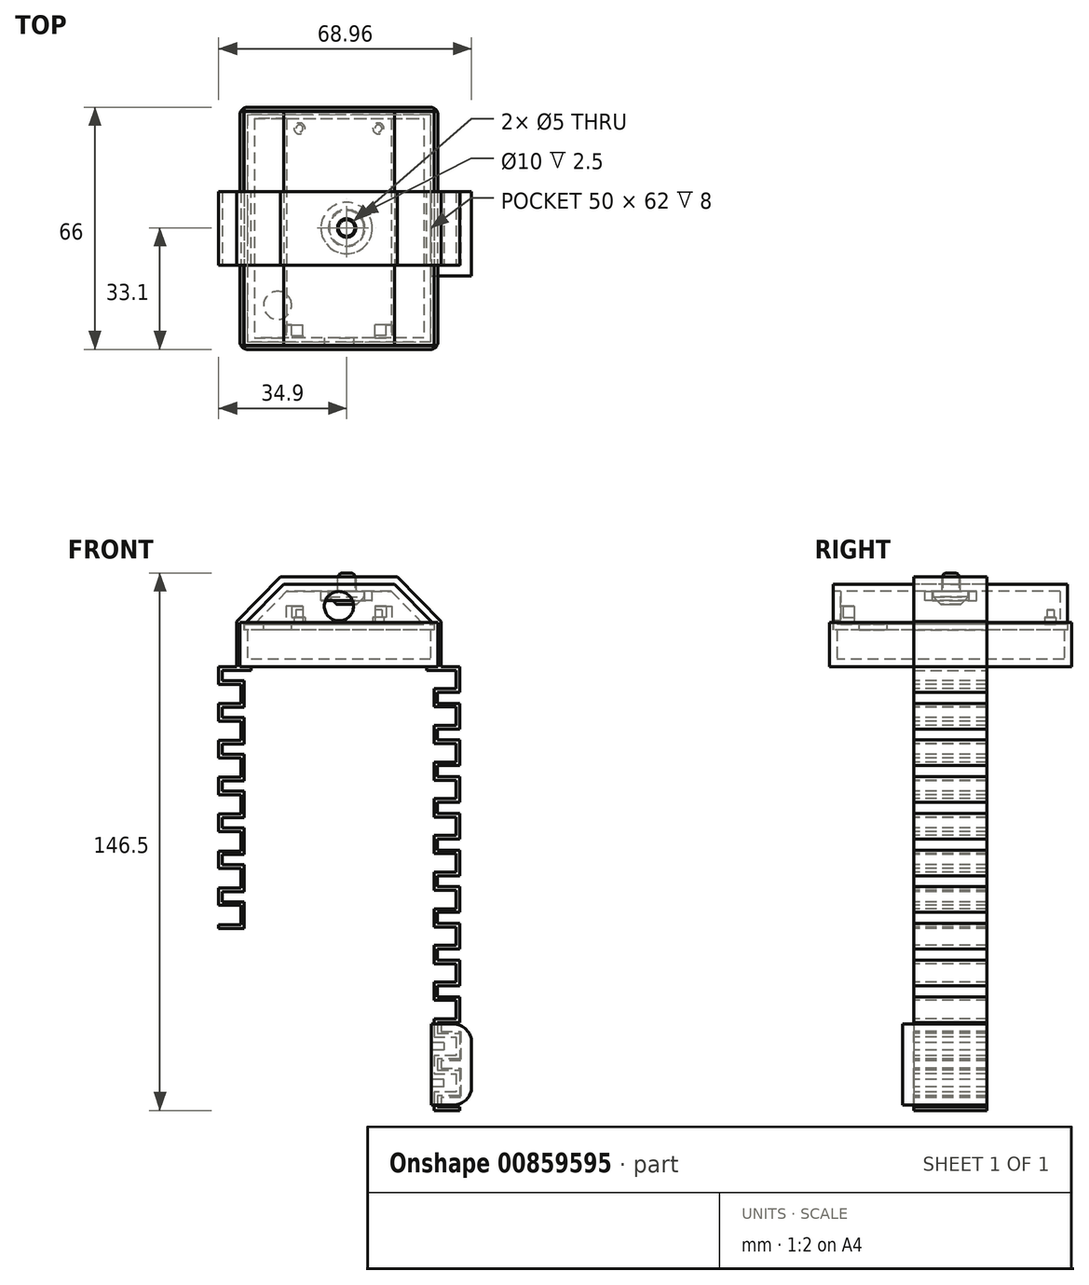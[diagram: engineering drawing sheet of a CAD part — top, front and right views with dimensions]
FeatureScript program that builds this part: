
annotation { "Feature Type Name" : "Feature", "Feature Type Description" : "" }
export const myFeature = defineFeature(function(context is Context, id is Id, definition is map)
    precondition{}
    {
        {
            var Q0;
            Q0=qCreatedBy(makeId("Top.planeOp"),FACE);
            var sketch = newSketch(context, id + "F0", { "sketchPlane" : qUnion([Q0])});
            skLineSegment(sketch, "E0.bottom", {"start": v(27, 33) * mm, "end": v(-27, 33) * mm});
            skLineSegment(sketch, "E0.top", {"start": v(27, -33) * mm, "end": v(-27, -33) * mm});
            skLineSegment(sketch, "E0.left", {"start": v(27, 33) * mm, "end": v(27, -33) * mm});
            skLineSegment(sketch, "E0.right", {"start": v(-27, 33) * mm, "end": v(-27, -33) * mm});
            skPoint(sketch, "E0.middle", {"position": v(0, 0) * mm});
            skSolve(sketch);
        }
        {
            var Q0;
            Q0 = qSketchRegion(id + "F0", true);
            extrude(context, id + "F1", {"entities" : qUnion([Q0]), "depth" : 12 * mm, "offsetDistance" : 25 * mm});
        }
        {
            var Q0;
            Q0=makeQuery(id+"F1.opExtrude","CAP_FACE",FACE,{"disambiguationData":[OSD([sQuery(id+"F0.wireOp",EDGE,"E0.bottom"),sQuery(id+"F0.wireOp",EDGE,"E0.top"),sQuery(id+"F0.wireOp",EDGE,"E0.left"),sQuery(id+"F0.wireOp",EDGE,"E0.right")])],"isStart":false});
            shell(context, id + "F2", {"entities" : qUnion([Q0]), "thickness" : 2 * mm});
        }
        {
            var Q0;
            Q0=makeQuery(id+"F1.opExtrude","CAP_FACE",FACE,{"disambiguationData":[OSD([sQuery(id+"F0.wireOp",EDGE,"E0.bottom"),sQuery(id+"F0.wireOp",EDGE,"E0.top"),sQuery(id+"F0.wireOp",EDGE,"E0.left"),sQuery(id+"F0.wireOp",EDGE,"E0.right")])],"isStart":false});
            var sketch = newSketch(context, id + "F3", { "sketchPlane" : qUnion([Q0])});
            skLineSegment(sketch, "E1.0", {"start": v(25, 31) * mm, "end": v(-25, 31) * mm});
            skLineSegment(sketch, "E2.0", {"start": v(-25, 31) * mm, "end": v(-25, -31) * mm});
            skLineSegment(sketch, "E3.0", {"start": v(25, -31) * mm, "end": v(-25, -31) * mm});
            skLineSegment(sketch, "E4.0", {"start": v(25, 31) * mm, "end": v(25, -31) * mm});
            skLineSegment(sketch, "E5.0", {"start": v(26, 32) * mm, "end": v(-26, 32) * mm});
            skLineSegment(sketch, "E5.1", {"start": v(26, 32) * mm, "end": v(26, -32) * mm});
            skLineSegment(sketch, "E5.2", {"start": v(26, -32) * mm, "end": v(-26, -32) * mm});
            skLineSegment(sketch, "E5.3", {"start": v(-26, 32) * mm, "end": v(-26, -32) * mm});
            skSolve(sketch);
        }
        {
            var Q0;
            Q0 = qSketchRegion(id + "F3", true);
            extrude(context, id + "F4", {"entities" : qUnion([Q0]), "operationType" : NewBodyOperationType.REMOVE, "oppositeDirection" : true, "depth" : 2 * mm, "offsetDistance" : 25 * mm});
        }
        {
            var Q0;
            Q0=makeQuery(id+"F4.boolean.opBoolean","COPY",FACE,{"derivedFrom":makeQuery(id+"F4.opExtrude","CAP_FACE",FACE,{"disambiguationData":[OSD([sQuery(id+"F3.wireOp",EDGE,"E1.0"),sQuery(id+"F3.wireOp",EDGE,"E2.0"),sQuery(id+"F3.wireOp",EDGE,"E3.0"),sQuery(id+"F3.wireOp",EDGE,"E4.0"),sQuery(id+"F3.wireOp",EDGE,"E5.0"),sQuery(id+"F3.wireOp",EDGE,"E5.1"),sQuery(id+"F3.wireOp",EDGE,"E5.2"),sQuery(id+"F3.wireOp",EDGE,"E5.3")])],"isStart":false})});
            var sketch = newSketch(context, id + "F5", { "sketchPlane" : qUnion([Q0])});
            skLineSegment(sketch, "E6.0", {"start": v(25.9, 31.9) * mm, "end": v(-25.9, 31.9) * mm});
            skLineSegment(sketch, "E6.1", {"start": v(25.9, 31.9) * mm, "end": v(25.9, -31.9) * mm});
            skLineSegment(sketch, "E6.2", {"start": v(25.9, -31.9) * mm, "end": v(-25.9, -31.9) * mm});
            skLineSegment(sketch, "E6.3", {"start": v(-25.9, 31.9) * mm, "end": v(-25.9, -31.9) * mm});
            skSolve(sketch);
        }
        {
            var Q0;
            Q0 = qSketchRegion(id + "F5", true);
            extrude(context, id + "F6", {"entities" : qUnion([Q0]), "depth" : 1.5 * mm, "offsetDistance" : 25 * mm});
        }
        {
            var Q0;
            Q0=makeQuery(id+"F6.opExtrude","CAP_FACE",FACE,{"disambiguationData":[OSD([sQuery(id+"F5.wireOp",EDGE,"E6.0"),sQuery(id+"F5.wireOp",EDGE,"E6.1"),sQuery(id+"F5.wireOp",EDGE,"E6.2"),sQuery(id+"F5.wireOp",EDGE,"E6.3")])],"isStart":false});
            var sketch = newSketch(context, id + "F7", { "sketchPlane" : qUnion([Q0])});
            skLineSegment(sketch, "E7.bottom", {"start": v(12.85, 29.25) * mm, "end": v(-12.85, 29.25) * mm, "construction": true});
            skLineSegment(sketch, "E7.top", {"start": v(12.85, -29.25) * mm, "end": v(-12.85, -29.25) * mm, "construction": true});
            skLineSegment(sketch, "E7.left", {"start": v(12.85, 29.25) * mm, "end": v(12.85, -29.25) * mm, "construction": true});
            skLineSegment(sketch, "E7.right", {"start": v(-12.85, 29.25) * mm, "end": v(-12.85, -29.25) * mm, "construction": true});
            skPoint(sketch, "E7.middle", {"position": v(0, 0) * mm});
            skCircle(sketch, "E8", {"center": v(-10.75, 27.25) * mm, "radius": 1.5 * mm});
            skCircle(sketch, "E9.MirrorC", {"center": v(10.75, 27.25) * mm, "radius": 1.5 * mm});
            skLineSegment(sketch, "E10.bottom", {"start": v(-12.85, -29.25) * mm, "end": v(-9.85, -29.25) * mm});
            skLineSegment(sketch, "E10.top", {"start": v(-12.85, -26.25) * mm, "end": v(-9.85, -26.25) * mm});
            skLineSegment(sketch, "E10.left", {"start": v(-12.85, -29.25) * mm, "end": v(-12.85, -26.25) * mm});
            skLineSegment(sketch, "E10.right", {"start": v(-9.85, -29.25) * mm, "end": v(-9.85, -26.25) * mm});
            skLineSegment(sketch, "E11.MirrorCS", {"start": v(12.85, -29.25) * mm, "end": v(9.85, -29.25) * mm});
            skLineSegment(sketch, "E12.MirrorCS", {"start": v(12.85, -29.25) * mm, "end": v(12.85, -26.25) * mm});
            skLineSegment(sketch, "E13.MirrorCS", {"start": v(-12.85, -29.25) * mm, "end": v(12.85, -29.25) * mm, "construction": true});
            skLineSegment(sketch, "E14.MirrorCS", {"start": v(12.85, -26.25) * mm, "end": v(9.85, -26.25) * mm});
            skLineSegment(sketch, "E15.MirrorCS", {"start": v(9.85, -29.25) * mm, "end": v(9.85, -26.25) * mm});
            skSolve(sketch);
        }
        {
            var Q0;
            Q0 = qSketchRegion(id + "F7", true);
            extrude(context, id + "F8", {"entities" : qUnion([Q0]), "operationType" : NewBodyOperationType.ADD, "depth" : 2 * mm, "offsetDistance" : 25 * mm});
        }
        {
            var Q0;
            Q0=makeQuery(id+"F6.opExtrude","CAP_FACE",FACE,{"disambiguationData":[OSD([sQuery(id+"F5.wireOp",EDGE,"E6.0"),sQuery(id+"F5.wireOp",EDGE,"E6.1"),sQuery(id+"F5.wireOp",EDGE,"E6.2"),sQuery(id+"F5.wireOp",EDGE,"E6.3")])],"isStart":false});
            var sketch = newSketch(context, id + "F9", { "sketchPlane" : qUnion([Q0])});
            skLineSegment(sketch, "E16.bottom", {"start": v(-12.85, -26.25) * mm, "end": v(-14.45, -26.25) * mm});
            skLineSegment(sketch, "E16.top", {"start": v(-9.85, -29.9) * mm, "end": v(-14.45, -29.9) * mm});
            skLineSegment(sketch, "E16.left", {"start": v(-9.85, -29.25) * mm, "end": v(-9.85, -29.9) * mm});
            skLineSegment(sketch, "E16.right", {"start": v(-14.45, -26.25) * mm, "end": v(-14.45, -29.9) * mm});
            skLineSegment(sketch, "E17.0", {"start": v(-12.85, -29.25) * mm, "end": v(-12.85, -26.25) * mm});
            skLineSegment(sketch, "E18.0", {"start": v(-12.85, -29.25) * mm, "end": v(-9.85, -29.25) * mm});
            skPoint(sketch, "E19.orphan", {"position": v(-9.85, -26.25) * mm});
            skLineSegment(sketch, "E20.MirrorCS", {"start": v(9.85, -29.25) * mm, "end": v(9.85, -29.9) * mm});
            skLineSegment(sketch, "E21.MirrorCS", {"start": v(14.45, -26.25) * mm, "end": v(14.45, -29.9) * mm});
            skLineSegment(sketch, "E22.MirrorCS", {"start": v(12.85, -29.25) * mm, "end": v(12.85, -26.25) * mm});
            skPoint(sketch, "E23.MirrorP", {"position": v(9.85, -26.25) * mm});
            skLineSegment(sketch, "E24.MirrorCS", {"start": v(9.85, -29.9) * mm, "end": v(14.45, -29.9) * mm});
            skLineSegment(sketch, "E25.MirrorCS", {"start": v(12.85, -26.25) * mm, "end": v(14.45, -26.25) * mm});
            skLineSegment(sketch, "E26.MirrorCS", {"start": v(12.85, -29.25) * mm, "end": v(9.85, -29.25) * mm});
            skSolve(sketch);
        }
        {
            var Q0;
            Q0 = qSketchRegion(id + "F9", true);
            extrude(context, id + "F10", {"entities" : qUnion([Q0]), "operationType" : NewBodyOperationType.ADD, "depth" : 5 * mm, "offsetDistance" : 25 * mm});
        }
        {
            var Q0;
            Q0=makeQuery(id+"F8.opExtrude","CAP_FACE",FACE,{"disambiguationData":[OSD([sQuery(id+"F7.wireOp",EDGE,"E8")])],"isStart":false});
            var sketch = newSketch(context, id + "F11", { "sketchPlane" : qUnion([Q0])});
            skCircle(sketch, "E27", {"center": v(-10.75, 27.25) * mm, "radius": 0.95 * mm});
            skCircle(sketch, "E28.MirrorC", {"center": v(10.75, 27.25) * mm, "radius": 0.95 * mm});
            skSolve(sketch);
        }
        {
            var Q0;
            Q0 = qSketchRegion(id + "F11", true);
            extrude(context, id + "F12", {"entities" : qUnion([Q0]), "operationType" : NewBodyOperationType.ADD, "depth" : 2 * mm, "offsetDistance" : 25 * mm});
        }
        {
            var Q0;
            Q0=makeQuery(id+"F6.opExtrude","SWEPT_FACE",FACE,{"disambiguationData":[OSD([sQuery(id+"F5.wireOp",EDGE,"E6.2")])]});
            var sketch = newSketch(context, id + "F13", { "sketchPlane" : qUnion([Q0])});
            skLineSegment(sketch, "E29.0", {"start": v(25.9, 11.5) * mm, "end": v(-25.9, 11.5) * mm});
            skLineSegment(sketch, "E30", {"start": v(-25.9, 11.5) * mm, "end": v(-15.12, 22.5) * mm});
            skLineSegment(sketch, "E31", {"start": v(-15.12, 22.5) * mm, "end": v(0, 22.5) * mm});
            skLineSegment(sketch, "E32.MirrorCS", {"start": v(15.12, 22.5) * mm, "end": v(0, 22.5) * mm});
            skLineSegment(sketch, "E33.MirrorCS", {"start": v(25.9, 11.5) * mm, "end": v(15.12, 22.5) * mm});
            skSolve(sketch);
        }
        {
            var Q0;
            Q0 = qSketchRegion(id + "F13", true);
            var Q1;
            Q1=makeQuery(id+"F6.opExtrude","SWEPT_FACE",FACE,{"disambiguationData":[OSD([sQuery(id+"F5.wireOp",EDGE,"E6.0")])]});
            extrude(context, id + "F14", {"entities" : qUnion([Q0]), "endBound" : BoundingType.UP_TO_SURFACE, "oppositeDirection" : true, "depth" : 25 * mm, "endBoundEntityFace" : qUnion([Q1]), "offsetDistance" : 25 * mm});
        }
        {
            var Q0;
            Q0=makeQuery(id+"F14.opExtrude","SWEPT_FACE",FACE,{"disambiguationData":[OSD([sQuery(id+"F13.wireOp",EDGE,"E29.0")])]});
            shell(context, id + "F15", {"entities" : qUnion([Q0]), "thickness" : 2 * mm});
        }
        {
            var Q0;
            Q0=makeQuery(id+"F6.opExtrude","CAP_FACE",FACE,{"disambiguationData":[OSD([sQuery(id+"F5.wireOp",EDGE,"E6.0"),sQuery(id+"F5.wireOp",EDGE,"E6.1"),sQuery(id+"F5.wireOp",EDGE,"E6.2"),sQuery(id+"F5.wireOp",EDGE,"E6.3")])],"isStart":false});
            var sketch = newSketch(context, id + "F16", { "sketchPlane" : qUnion([Q0])});
            skCircle(sketch, "E34", {"center": v(-16.73, -20.99) * mm, "radius": 3.81 * mm});
            skSolve(sketch);
        }
        {
            var Q0;
            Q0 = qSketchRegion(id + "F16", true);
            extrude(context, id + "F17", {"entities" : qUnion([Q0]), "operationType" : NewBodyOperationType.REMOVE, "endBound" : BoundingType.UP_TO_NEXT, "oppositeDirection" : true, "depth" : 25 * mm, "offsetDistance" : 25 * mm});
        }
        {
            var Q0;
            Q0=makeQuery(id+"F1.opExtrude","SWEPT_EDGE",EDGE,{"disambiguationData":[OSD([sQuery(id+"F0.wireOp",EDGE,"E0.bottom"),sQuery(id+"F0.wireOp",EDGE,"E0.right")])]});
            var Q1;
            Q1=makeQuery(id+"F1.opExtrude","SWEPT_EDGE",EDGE,{"disambiguationData":[OSD([sQuery(id+"F0.wireOp",EDGE,"E0.bottom"),sQuery(id+"F0.wireOp",EDGE,"E0.left")])]});
            var Q2;
            Q2=makeQuery(id+"F1.opExtrude","SWEPT_EDGE",EDGE,{"disambiguationData":[OSD([sQuery(id+"F0.wireOp",EDGE,"E0.top"),sQuery(id+"F0.wireOp",EDGE,"E0.left")])]});
            var Q3;
            Q3=makeQuery(id+"F1.opExtrude","SWEPT_EDGE",EDGE,{"disambiguationData":[OSD([sQuery(id+"F0.wireOp",EDGE,"E0.top"),sQuery(id+"F0.wireOp",EDGE,"E0.right")])]});
            fillet(context, id + "F18", {"entities" : qUnion([Q0, Q1, Q2, Q3]), "radius" : 2 * mm, "tangentPropagation" : true, "allowEdgeOverflow" : false});
        }
        {
            var Q0;
            Q0=makeQuery(id+"F0.imprint","IMPRINT",FACE,{"disambiguationData":[TD([[makeQuery(id+"F0.imprint","IMPRINT",EDGE,{"derivedFrom":sQuery(id+"F0.wireOp",EDGE,"E0.bottom")}),1.0]])]});
            var sketch = newSketch(context, id + "F19", { "sketchPlane" : qUnion([Q0])});
            skLineSegment(sketch, "E35.0", {"start": v(27, 10) * mm, "end": v(27, -10) * mm});
            skLineSegment(sketch, "E36.0", {"start": v(-27, 10) * mm, "end": v(-27, -10) * mm});
            skLineSegment(sketch, "E37.0", {"start": v(-25.9, 10) * mm, "end": v(-25.9, -10) * mm});
            skLineSegment(sketch, "E38.0", {"start": v(25.9, 10) * mm, "end": v(25.9, -10) * mm});
            skLineSegment(sketch, "E39", {"start": v(-27, -10) * mm, "end": v(-25.9, -10) * mm});
            skLineSegment(sketch, "E40", {"start": v(-27, 10) * mm, "end": v(-25.9, 10) * mm});
            skLineSegment(sketch, "E41.trimOffspring", {"start": v(25.9, -10) * mm, "end": v(27, -10) * mm});
            skLineSegment(sketch, "E42.trimOffspring", {"start": v(25.9, 10) * mm, "end": v(27, 10) * mm});
            skPoint(sketch, "E43.orphan", {"position": v(-25.9, 31.9) * mm});
            skPoint(sketch, "E44.orphan", {"position": v(-27, 33) * mm});
            skPoint(sketch, "E45.orphan", {"position": v(-27, -33) * mm});
            skPoint(sketch, "E46.orphan", {"position": v(-25.9, -31.9) * mm});
            skPoint(sketch, "E47.orphan", {"position": v(27, -33) * mm});
            skPoint(sketch, "E48.orphan", {"position": v(25.9, -31.9) * mm});
            skPoint(sketch, "E49.orphan", {"position": v(27, 33) * mm});
            skPoint(sketch, "E50.orphan", {"position": v(25.9, 31.9) * mm});
            skSolve(sketch);
        }
        {
            var Q0;
            Q0 = qSketchRegion(id + "F19", true);
            extrude(context, id + "F20", {"entities" : qUnion([Q0]), "operationType" : NewBodyOperationType.REMOVE, "endBound" : BoundingType.THROUGH_ALL, "depth" : 25 * mm, "offsetDistance" : 25 * mm});
        }
        {
            var Q0;
            Q0=makeQuery(id+"F20.boolean.opBoolean","COPY",FACE,{"derivedFrom":makeQuery(id+"F20.opExtrude","SWEPT_FACE",FACE,{"disambiguationData":[OSD([sQuery(id+"F19.wireOp",EDGE,"E39")])]})});
            var sketch = newSketch(context, id + "F21", { "sketchPlane" : qUnion([Q0])});
            skLineSegment(sketch, "E51.0", {"start": v(-15.12, 22.5) * mm, "end": v(-25.9, 11.5) * mm});
            skLineSegment(sketch, "E52.0", {"start": v(15.12, 22.5) * mm, "end": v(-15.12, 22.5) * mm});
            skLineSegment(sketch, "E53.0", {"start": v(15.12, 22.5) * mm, "end": v(25.9, 11.5) * mm});
            skLineSegment(sketch, "E54.0", {"start": v(25.9, 10) * mm, "end": v(25.9, 0) * mm});
            skLineSegment(sketch, "E55.0", {"start": v(-25.9, 10) * mm, "end": v(-25.9, 0) * mm});
            skLineSegment(sketch, "E56", {"start": v(-25.9, 11.5) * mm, "end": v(-25.9, 10) * mm});
            skLineSegment(sketch, "E57", {"start": v(25.9, 11.5) * mm, "end": v(25.9, 10) * mm});
            skLineSegment(sketch, "E58", {"start": v(-25.9, 0) * mm, "end": v(-27.9, 0) * mm});
            skLineSegment(sketch, "E59.0", {"start": v(-27.9, 10) * mm, "end": v(-27.9, 0) * mm});
            skLineSegment(sketch, "E59.1", {"start": v(-27.9, 12.32) * mm, "end": v(-27.9, 10) * mm});
            skLineSegment(sketch, "E59.2", {"start": v(-15.96, 24.5) * mm, "end": v(-27.9, 12.32) * mm});
            skLineSegment(sketch, "E59.3", {"start": v(27.9, 10) * mm, "end": v(27.9, 0) * mm});
            skLineSegment(sketch, "E59.4", {"start": v(27.9, 12.32) * mm, "end": v(27.9, 10) * mm});
            skLineSegment(sketch, "E59.5", {"start": v(15.96, 24.5) * mm, "end": v(27.9, 12.32) * mm});
            skLineSegment(sketch, "E59.6", {"start": v(15.96, 24.5) * mm, "end": v(-15.96, 24.5) * mm});
            skLineSegment(sketch, "E60", {"start": v(25.9, 0) * mm, "end": v(27.9, 0) * mm});
            skSolve(sketch);
        }
        {
            var Q0;
            Q0 = qSketchRegion(id + "F21", true);
            var Q1;
            Q1=makeQuery(id+"F20.boolean.opBoolean","COPY",FACE,{"derivedFrom":makeQuery(id+"F20.opExtrude","SWEPT_FACE",FACE,{"disambiguationData":[OSD([sQuery(id+"F19.wireOp",EDGE,"E40")])]})});
            extrude(context, id + "F22", {"entities" : qUnion([Q0]), "endBound" : BoundingType.UP_TO_SURFACE, "depth" : 25 * mm, "endBoundEntityFace" : qUnion([Q1]), "offsetDistance" : 25 * mm});
        }
        {
            var Q0;
            Q0=makeQuery(id+"F14.opExtrude","CAP_FACE",FACE,{"disambiguationData":[OSD([sQuery(id+"F13.wireOp",EDGE,"E29.0"),sQuery(id+"F13.wireOp",EDGE,"E30"),sQuery(id+"F13.wireOp",EDGE,"E31"),sQuery(id+"F13.wireOp",EDGE,"E32.MirrorCS"),sQuery(id+"F13.wireOp",EDGE,"E33.MirrorCS")])],"isStart":true});
            var sketch = newSketch(context, id + "F23", { "sketchPlane" : qUnion([Q0])});
            skCircle(sketch, "E61", {"center": v(0, 16.5) * mm, "radius": 4 * mm});
            skSolve(sketch);
        }
        {
            var Q0;
            Q0 = qSketchRegion(id + "F23", true);
            var Q1;
            {var subQ0=sQuery(id+"F13.wireOp",EDGE,"E33.MirrorCS");var subQ1=sQuery(id+"F13.wireOp",EDGE,"E32.MirrorCS");var subQ2=sQuery(id+"F13.wireOp",EDGE,"E31");var subQ3=sQuery(id+"F13.wireOp",EDGE,"E30");var subQ4=sQuery(id+"F13.wireOp",EDGE,"E29.0");Q1=makeQuery(id+"F15.opShell","OFFSET_FACE",FACE,{"disambiguationData":[OSD([subQ4,subQ3,subQ2,subQ1,subQ0]),TDD([makeQuery(id+"F14.opExtrude","CAP_FACE",FACE,{"disambiguationData":[OSD([subQ4,subQ3,subQ2,subQ1,subQ0])],"isStart":true})])]});}
            extrude(context, id + "F24", {"entities" : qUnion([Q0]), "operationType" : NewBodyOperationType.REMOVE, "endBound" : BoundingType.UP_TO_SURFACE, "oppositeDirection" : true, "depth" : 25 * mm, "endBoundEntityFace" : qUnion([Q1]), "offsetDistance" : 25 * mm});
        }
        {
            var Q0;
            Q0=makeQuery(id+"F15.opShell","OFFSET_FACE",FACE,{"disambiguationData":[OSD([sQuery(id+"F13.wireOp",EDGE,"E31"),sQuery(id+"F13.wireOp",EDGE,"E32.MirrorCS")])]});
            var sketch = newSketch(context, id + "F25", { "sketchPlane" : qUnion([Q0])});
            skLineSegment(sketch, "E62.0", {"start": v(-25.9, -31.9) * mm, "end": v(-25.9, 31.9) * mm, "construction": true});
            skLineSegment(sketch, "E63.0", {"start": v(25.9, 31.9) * mm, "end": v(-25.9, 31.9) * mm, "construction": true});
            skCircle(sketch, "E64", {"center": v(2.1, -0.1) * mm, "radius": 2.5 * mm});
            skSolve(sketch);
        }
        {
            var Q0;
            Q0 = qSketchRegion(id + "F25", true);
            extrude(context, id + "F26", {"entities" : qUnion([Q0]), "operationType" : NewBodyOperationType.REMOVE, "endBound" : BoundingType.THROUGH_ALL, "oppositeDirection" : true, "depth" : 25 * mm, "offsetDistance" : 25 * mm});
        }
        {
            var Q0;
            Q0=makeQuery(id+"F15.opShell","OFFSET_FACE",FACE,{"disambiguationData":[OSD([sQuery(id+"F13.wireOp",EDGE,"E31"),sQuery(id+"F13.wireOp",EDGE,"E32.MirrorCS")])]});
            var sketch = newSketch(context, id + "F27", { "sketchPlane" : qUnion([Q0])});
            skCircle(sketch, "E65", {"center": v(2.1, -0.1) * mm, "radius": 5 * mm});
            skCircle(sketch, "E66", {"center": v(2.1, -0.1) * mm, "radius": 7 * mm});
            skSolve(sketch);
        }
        {
            var Q0;
            Q0 = qSketchRegion(id + "F27", true);
            extrude(context, id + "F28", {"entities" : qUnion([Q0]), "operationType" : NewBodyOperationType.ADD, "depth" : 2.5 * mm, "offsetDistance" : 25 * mm});
        }
        {
            var Q0;
            Q0=makeQuery(id+"F22.opExtrude","CAP_FACE",FACE,{"disambiguationData":[OSD([sQuery(id+"F21.wireOp",EDGE,"E51.0"),sQuery(id+"F21.wireOp",EDGE,"E52.0"),sQuery(id+"F21.wireOp",EDGE,"E53.0"),sQuery(id+"F21.wireOp",EDGE,"E54.0"),sQuery(id+"F21.wireOp",EDGE,"E55.0"),sQuery(id+"F21.wireOp",EDGE,"E56"),sQuery(id+"F21.wireOp",EDGE,"E57"),sQuery(id+"F21.wireOp",EDGE,"E58"),sQuery(id+"F21.wireOp",EDGE,"E59.0"),sQuery(id+"F21.wireOp",EDGE,"E59.1"),sQuery(id+"F21.wireOp",EDGE,"E59.2"),sQuery(id+"F21.wireOp",EDGE,"E59.3"),sQuery(id+"F21.wireOp",EDGE,"E59.4"),sQuery(id+"F21.wireOp",EDGE,"E59.5"),sQuery(id+"F21.wireOp",EDGE,"E59.6"),sQuery(id+"F21.wireOp",EDGE,"E60")])],"isStart":true});
            var sketch = newSketch(context, id + "F29", { "sketchPlane" : qUnion([Q0])});
            skLineSegment(sketch, "E67.0", {"start": v(25.9, 0) * mm, "end": v(27.9, 0) * mm});
            skLineSegment(sketch, "E68", {"start": v(27.9, 0) * mm, "end": v(32.9, 0) * mm});
            skLineSegment(sketch, "E69", {"start": v(25.9, 0) * mm, "end": v(25.9, -1) * mm});
            skLineSegment(sketch, "E70", {"start": v(25.9, -1) * mm, "end": v(31.9, -1) * mm});
            skLineSegment(sketch, "E71", {"start": v(32.9, 0) * mm, "end": v(32.9, -7) * mm});
            skLineSegment(sketch, "E72", {"start": v(31.9, -1) * mm, "end": v(31.9, -6) * mm});
            skLineSegment(sketch, "E73", {"start": v(31.9, -6) * mm, "end": v(25.9, -6) * mm});
            skLineSegment(sketch, "E74", {"start": v(32.9, -7) * mm, "end": v(26.9, -7) * mm});
            skLineSegment(sketch, "E75", {"start": v(25.9, -6) * mm, "end": v(25.9, -11) * mm});
            skLineSegment(sketch, "E76", {"start": v(25.9, -11) * mm, "end": v(31.9, -11) * mm});
            skLineSegment(sketch, "E77", {"start": v(26.9, -7) * mm, "end": v(26.9, -10) * mm});
            skLineSegment(sketch, "E78", {"start": v(26.9, -10) * mm, "end": v(32.9, -10) * mm});
            skLineSegment(sketch, "E79.1.0.0", {"start": v(31.9, -11) * mm, "end": v(31.9, -16) * mm});
            skLineSegment(sketch, "E79.1.0.1", {"start": v(32.9, -10) * mm, "end": v(32.9, -17) * mm});
            skLineSegment(sketch, "E79.1.0.2", {"start": v(32.9, -17) * mm, "end": v(26.9, -17) * mm});
            skLineSegment(sketch, "E79.1.0.3", {"start": v(31.9, -16) * mm, "end": v(25.9, -16) * mm});
            skLineSegment(sketch, "E79.1.0.4", {"start": v(25.9, -16) * mm, "end": v(25.9, -21) * mm});
            skLineSegment(sketch, "E79.1.0.5", {"start": v(26.9, -17) * mm, "end": v(26.9, -20) * mm});
            skLineSegment(sketch, "E79.1.0.6", {"start": v(26.9, -20) * mm, "end": v(32.9, -20) * mm});
            skLineSegment(sketch, "E79.1.0.7", {"start": v(25.9, -21) * mm, "end": v(31.9, -21) * mm});
            skLineSegment(sketch, "E79.2.0.0", {"start": v(31.9, -21) * mm, "end": v(31.9, -26) * mm});
            skLineSegment(sketch, "E79.2.0.1", {"start": v(32.9, -20) * mm, "end": v(32.9, -27) * mm});
            skLineSegment(sketch, "E79.2.0.2", {"start": v(32.9, -27) * mm, "end": v(26.9, -27) * mm});
            skLineSegment(sketch, "E79.2.0.3", {"start": v(31.9, -26) * mm, "end": v(25.9, -26) * mm});
            skLineSegment(sketch, "E79.2.0.4", {"start": v(25.9, -26) * mm, "end": v(25.9, -31) * mm});
            skLineSegment(sketch, "E79.2.0.5", {"start": v(26.9, -27) * mm, "end": v(26.9, -30) * mm});
            skLineSegment(sketch, "E79.2.0.6", {"start": v(26.9, -30) * mm, "end": v(32.9, -30) * mm});
            skLineSegment(sketch, "E79.2.0.7", {"start": v(25.9, -31) * mm, "end": v(31.9, -31) * mm});
            skLineSegment(sketch, "E79.direction1", {"start": v(31.9, -6) * mm, "end": v(31.9, -16) * mm, "construction": true});
            skLineSegment(sketch, "E80.0.3.0", {"start": v(31.9, -31) * mm, "end": v(31.9, -36) * mm});
            skLineSegment(sketch, "E80.3.3.0", {"start": v(32.9, -30) * mm, "end": v(32.9, -37) * mm});
            skLineSegment(sketch, "E80.6.3.0", {"start": v(32.9, -37) * mm, "end": v(26.9, -37) * mm});
            skLineSegment(sketch, "E80.9.3.0", {"start": v(31.9, -36) * mm, "end": v(25.9, -36) * mm});
            skLineSegment(sketch, "E80.12.3.0", {"start": v(25.9, -36) * mm, "end": v(25.9, -41) * mm});
            skLineSegment(sketch, "E80.15.3.0", {"start": v(26.9, -37) * mm, "end": v(26.9, -40) * mm});
            skLineSegment(sketch, "E80.18.3.0", {"start": v(26.9, -40) * mm, "end": v(32.9, -40) * mm});
            skLineSegment(sketch, "E80.21.3.0", {"start": v(25.9, -41) * mm, "end": v(31.9, -41) * mm});
            skLineSegment(sketch, "E80.0.4.0", {"start": v(31.9, -41) * mm, "end": v(31.9, -46) * mm});
            skLineSegment(sketch, "E80.3.4.0", {"start": v(32.9, -40) * mm, "end": v(32.9, -47) * mm});
            skLineSegment(sketch, "E80.6.4.0", {"start": v(32.9, -47) * mm, "end": v(26.9, -47) * mm});
            skLineSegment(sketch, "E80.9.4.0", {"start": v(31.9, -46) * mm, "end": v(25.9, -46) * mm});
            skLineSegment(sketch, "E80.12.4.0", {"start": v(25.9, -46) * mm, "end": v(25.9, -51) * mm});
            skLineSegment(sketch, "E80.15.4.0", {"start": v(26.9, -47) * mm, "end": v(26.9, -50) * mm});
            skLineSegment(sketch, "E80.18.4.0", {"start": v(26.9, -50) * mm, "end": v(32.9, -50) * mm});
            skLineSegment(sketch, "E80.21.4.0", {"start": v(25.9, -51) * mm, "end": v(31.9, -51) * mm});
            skLineSegment(sketch, "E80.0.5.0", {"start": v(31.9, -51) * mm, "end": v(31.9, -56) * mm});
            skLineSegment(sketch, "E80.3.5.0", {"start": v(32.9, -50) * mm, "end": v(32.9, -57) * mm});
            skLineSegment(sketch, "E80.6.5.0", {"start": v(32.9, -57) * mm, "end": v(26.9, -57) * mm});
            skLineSegment(sketch, "E80.9.5.0", {"start": v(31.9, -56) * mm, "end": v(25.9, -56) * mm});
            skLineSegment(sketch, "E80.12.5.0", {"start": v(25.9, -56) * mm, "end": v(25.9, -61) * mm});
            skLineSegment(sketch, "E80.15.5.0", {"start": v(26.9, -57) * mm, "end": v(26.9, -60) * mm});
            skLineSegment(sketch, "E80.18.5.0", {"start": v(26.9, -60) * mm, "end": v(32.9, -60) * mm});
            skLineSegment(sketch, "E80.21.5.0", {"start": v(25.9, -61) * mm, "end": v(31.9, -61) * mm});
            skLineSegment(sketch, "E80.0.6.0", {"start": v(31.9, -61) * mm, "end": v(31.9, -66) * mm});
            skLineSegment(sketch, "E80.3.6.0", {"start": v(32.9, -60) * mm, "end": v(32.9, -67) * mm});
            skLineSegment(sketch, "E80.6.6.0", {"start": v(32.9, -67) * mm, "end": v(26.9, -67) * mm});
            skLineSegment(sketch, "E80.9.6.0", {"start": v(31.9, -66) * mm, "end": v(25.9, -66) * mm});
            skLineSegment(sketch, "E80.12.6.0", {"start": v(25.9, -66) * mm, "end": v(25.9, -71) * mm});
            skLineSegment(sketch, "E80.15.6.0", {"start": v(26.9, -67) * mm, "end": v(26.9, -70) * mm});
            skLineSegment(sketch, "E80.18.6.0", {"start": v(26.9, -70) * mm, "end": v(32.9, -70) * mm});
            skLineSegment(sketch, "E80.21.6.0", {"start": v(25.9, -71) * mm, "end": v(31.9, -71) * mm});
            skLineSegment(sketch, "E80.0.7.0", {"start": v(31.9, -71) * mm, "end": v(31.9, -76) * mm});
            skLineSegment(sketch, "E80.3.7.0", {"start": v(32.9, -70) * mm, "end": v(32.9, -77) * mm});
            skLineSegment(sketch, "E80.6.7.0", {"start": v(32.9, -77) * mm, "end": v(26.9, -77) * mm});
            skLineSegment(sketch, "E80.9.7.0", {"start": v(31.9, -76) * mm, "end": v(25.9, -76) * mm});
            skLineSegment(sketch, "E80.12.7.0", {"start": v(25.9, -76) * mm, "end": v(25.9, -81) * mm});
            skLineSegment(sketch, "E80.15.7.0", {"start": v(26.9, -77) * mm, "end": v(26.9, -80) * mm});
            skLineSegment(sketch, "E80.18.7.0", {"start": v(26.9, -80) * mm, "end": v(32.9, -80) * mm});
            skLineSegment(sketch, "E80.21.7.0", {"start": v(25.9, -81) * mm, "end": v(31.9, -81) * mm});
            skLineSegment(sketch, "E81", {"start": v(32.9, -80) * mm, "end": v(32.9, -81) * mm});
            skLineSegment(sketch, "E82", {"start": v(32.9, -81) * mm, "end": v(31.9, -81) * mm});
            skLineSegment(sketch, "E83", {"start": v(-25.9, 0) * mm, "end": v(-25.9, -1) * mm});
            skLineSegment(sketch, "E84", {"start": v(-25.9, -1) * mm, "end": v(-31.8, -1) * mm});
            skLineSegment(sketch, "E85", {"start": v(-31.8, -1) * mm, "end": v(-31.8, -3.8) * mm});
            skLineSegment(sketch, "E86", {"start": v(-31.8, -3.8) * mm, "end": v(-25.8, -3.8) * mm});
            skLineSegment(sketch, "E87", {"start": v(-25.8, -3.8) * mm, "end": v(-25.8, -11.05) * mm});
            skLineSegment(sketch, "E88", {"start": v(-27.9, 0) * mm, "end": v(-32.8, 0) * mm});
            skLineSegment(sketch, "E89", {"start": v(-32.8, 0) * mm, "end": v(-32.8, -4.8) * mm});
            skLineSegment(sketch, "E90", {"start": v(-32.8, -4.8) * mm, "end": v(-26.8, -4.8) * mm});
            skLineSegment(sketch, "E91", {"start": v(-26.8, -4.8) * mm, "end": v(-26.8, -10.05) * mm});
            skLineSegment(sketch, "E92", {"start": v(-26.8, -10.05) * mm, "end": v(-32.8, -10.05) * mm});
            skLineSegment(sketch, "E93", {"start": v(-25.8, -11.05) * mm, "end": v(-31.8, -11.05) * mm});
            skLineSegment(sketch, "E94.1.0.0", {"start": v(-32.8, -10.05) * mm, "end": v(-32.8, -14.85) * mm});
            skLineSegment(sketch, "E94.1.0.1", {"start": v(-31.8, -11.05) * mm, "end": v(-31.8, -13.85) * mm});
            skLineSegment(sketch, "E94.1.0.2", {"start": v(-31.8, -13.85) * mm, "end": v(-25.8, -13.85) * mm});
            skLineSegment(sketch, "E94.1.0.3", {"start": v(-32.8, -14.85) * mm, "end": v(-26.8, -14.85) * mm});
            skLineSegment(sketch, "E94.1.0.4", {"start": v(-25.8, -13.85) * mm, "end": v(-25.8, -21.1) * mm});
            skLineSegment(sketch, "E94.1.0.5", {"start": v(-26.8, -14.85) * mm, "end": v(-26.8, -20.1) * mm});
            skLineSegment(sketch, "E94.1.0.6", {"start": v(-26.8, -20.1) * mm, "end": v(-32.8, -20.1) * mm});
            skLineSegment(sketch, "E94.1.0.7", {"start": v(-25.8, -21.1) * mm, "end": v(-31.8, -21.1) * mm});
            skLineSegment(sketch, "E94.2.0.0", {"start": v(-32.8, -20.1) * mm, "end": v(-32.8, -24.9) * mm});
            skLineSegment(sketch, "E94.2.0.1", {"start": v(-31.8, -21.1) * mm, "end": v(-31.8, -23.9) * mm});
            skLineSegment(sketch, "E94.2.0.2", {"start": v(-31.8, -23.9) * mm, "end": v(-25.8, -23.9) * mm});
            skLineSegment(sketch, "E94.2.0.3", {"start": v(-32.8, -24.9) * mm, "end": v(-26.8, -24.9) * mm});
            skLineSegment(sketch, "E94.2.0.4", {"start": v(-25.8, -23.9) * mm, "end": v(-25.8, -31.15) * mm});
            skLineSegment(sketch, "E94.2.0.5", {"start": v(-26.8, -24.9) * mm, "end": v(-26.8, -30.15) * mm});
            skLineSegment(sketch, "E94.2.0.6", {"start": v(-26.8, -30.15) * mm, "end": v(-32.8, -30.15) * mm});
            skLineSegment(sketch, "E94.2.0.7", {"start": v(-25.8, -31.15) * mm, "end": v(-31.8, -31.15) * mm});
            skLineSegment(sketch, "E94.direction1", {"start": v(-32.8, -4.8) * mm, "end": v(-32.8, -14.85) * mm, "construction": true});
            skLineSegment(sketch, "E95.0.3.0", {"start": v(-32.8, -30.15) * mm, "end": v(-32.8, -34.95) * mm});
            skLineSegment(sketch, "E95.3.3.0", {"start": v(-31.8, -31.15) * mm, "end": v(-31.8, -33.95) * mm});
            skLineSegment(sketch, "E95.6.3.0", {"start": v(-31.8, -33.95) * mm, "end": v(-25.8, -33.95) * mm});
            skLineSegment(sketch, "E95.9.3.0", {"start": v(-32.8, -34.95) * mm, "end": v(-26.8, -34.95) * mm});
            skLineSegment(sketch, "E95.12.3.0", {"start": v(-25.8, -33.95) * mm, "end": v(-25.8, -41.2) * mm});
            skLineSegment(sketch, "E95.15.3.0", {"start": v(-26.8, -34.95) * mm, "end": v(-26.8, -40.2) * mm});
            skLineSegment(sketch, "E95.18.3.0", {"start": v(-26.8, -40.2) * mm, "end": v(-32.8, -40.2) * mm});
            skLineSegment(sketch, "E95.21.3.0", {"start": v(-25.8, -41.2) * mm, "end": v(-31.8, -41.2) * mm});
            skLineSegment(sketch, "E95.0.4.0", {"start": v(-32.8, -40.2) * mm, "end": v(-32.8, -45) * mm});
            skLineSegment(sketch, "E95.3.4.0", {"start": v(-31.8, -41.2) * mm, "end": v(-31.8, -44) * mm});
            skLineSegment(sketch, "E95.6.4.0", {"start": v(-31.8, -44) * mm, "end": v(-25.8, -44) * mm});
            skLineSegment(sketch, "E95.9.4.0", {"start": v(-32.8, -45) * mm, "end": v(-26.8, -45) * mm});
            skLineSegment(sketch, "E95.12.4.0", {"start": v(-25.8, -44) * mm, "end": v(-25.8, -51.25) * mm});
            skLineSegment(sketch, "E95.15.4.0", {"start": v(-26.8, -45) * mm, "end": v(-26.8, -50.25) * mm});
            skLineSegment(sketch, "E95.18.4.0", {"start": v(-26.8, -50.25) * mm, "end": v(-32.8, -50.25) * mm});
            skLineSegment(sketch, "E95.21.4.0", {"start": v(-25.8, -51.25) * mm, "end": v(-31.8, -51.25) * mm});
            skLineSegment(sketch, "E95.0.5.0", {"start": v(-32.8, -50.25) * mm, "end": v(-32.8, -55.05) * mm});
            skLineSegment(sketch, "E95.3.5.0", {"start": v(-31.8, -51.25) * mm, "end": v(-31.8, -54.05) * mm});
            skLineSegment(sketch, "E95.6.5.0", {"start": v(-31.8, -54.05) * mm, "end": v(-25.8, -54.05) * mm});
            skLineSegment(sketch, "E95.9.5.0", {"start": v(-32.8, -55.05) * mm, "end": v(-26.8, -55.05) * mm});
            skLineSegment(sketch, "E95.12.5.0", {"start": v(-25.8, -54.05) * mm, "end": v(-25.8, -61.3) * mm});
            skLineSegment(sketch, "E95.15.5.0", {"start": v(-26.8, -55.05) * mm, "end": v(-26.8, -60.3) * mm});
            skLineSegment(sketch, "E95.18.5.0", {"start": v(-26.8, -60.3) * mm, "end": v(-32.8, -60.3) * mm});
            skLineSegment(sketch, "E95.21.5.0", {"start": v(-25.8, -61.3) * mm, "end": v(-31.8, -61.3) * mm});
            skLineSegment(sketch, "E96.0.8.0", {"start": v(31.9, -81) * mm, "end": v(31.9, -86) * mm});
            skLineSegment(sketch, "E96.3.8.0", {"start": v(32.9, -80) * mm, "end": v(32.9, -87) * mm});
            skLineSegment(sketch, "E96.6.8.0", {"start": v(32.9, -87) * mm, "end": v(26.9, -87) * mm});
            skLineSegment(sketch, "E96.9.8.0", {"start": v(31.9, -86) * mm, "end": v(25.9, -86) * mm});
            skLineSegment(sketch, "E96.12.8.0", {"start": v(25.9, -86) * mm, "end": v(25.9, -91) * mm});
            skLineSegment(sketch, "E96.15.8.0", {"start": v(26.9, -87) * mm, "end": v(26.9, -90) * mm});
            skLineSegment(sketch, "E96.18.8.0", {"start": v(26.9, -90) * mm, "end": v(32.9, -90) * mm});
            skLineSegment(sketch, "E96.21.8.0", {"start": v(25.9, -91) * mm, "end": v(31.9, -91) * mm});
            skLineSegment(sketch, "E96.0.9.0", {"start": v(31.9, -91) * mm, "end": v(31.9, -96) * mm});
            skLineSegment(sketch, "E96.3.9.0", {"start": v(32.9, -90) * mm, "end": v(32.9, -97) * mm});
            skLineSegment(sketch, "E96.6.9.0", {"start": v(32.9, -97) * mm, "end": v(26.9, -97) * mm});
            skLineSegment(sketch, "E96.9.9.0", {"start": v(31.9, -96) * mm, "end": v(25.9, -96) * mm});
            skLineSegment(sketch, "E96.12.9.0", {"start": v(25.9, -96) * mm, "end": v(25.9, -101) * mm});
            skLineSegment(sketch, "E96.15.9.0", {"start": v(26.9, -97) * mm, "end": v(26.9, -100) * mm});
            skLineSegment(sketch, "E96.18.9.0", {"start": v(26.9, -100) * mm, "end": v(32.9, -100) * mm});
            skLineSegment(sketch, "E96.21.9.0", {"start": v(25.9, -101) * mm, "end": v(31.9, -101) * mm});
            skLineSegment(sketch, "E96.0.10.0", {"start": v(31.9, -101) * mm, "end": v(31.9, -106) * mm});
            skLineSegment(sketch, "E96.3.10.0", {"start": v(32.9, -100) * mm, "end": v(32.9, -107) * mm});
            skLineSegment(sketch, "E96.6.10.0", {"start": v(32.9, -107) * mm, "end": v(26.9, -107) * mm});
            skLineSegment(sketch, "E96.9.10.0", {"start": v(31.9, -106) * mm, "end": v(25.9, -106) * mm});
            skLineSegment(sketch, "E96.12.10.0", {"start": v(25.9, -106) * mm, "end": v(25.9, -111) * mm});
            skLineSegment(sketch, "E96.15.10.0", {"start": v(26.9, -107) * mm, "end": v(26.9, -110) * mm});
            skLineSegment(sketch, "E96.18.10.0", {"start": v(26.9, -110) * mm, "end": v(32.9, -110) * mm});
            skLineSegment(sketch, "E96.21.10.0", {"start": v(25.9, -111) * mm, "end": v(31.9, -111) * mm});
            skLineSegment(sketch, "E96.0.11.0", {"start": v(31.9, -111) * mm, "end": v(31.9, -116) * mm});
            skLineSegment(sketch, "E96.3.11.0", {"start": v(32.9, -110) * mm, "end": v(32.9, -117) * mm});
            skLineSegment(sketch, "E96.6.11.0", {"start": v(32.9, -117) * mm, "end": v(26.9, -117) * mm});
            skLineSegment(sketch, "E96.9.11.0", {"start": v(31.9, -116) * mm, "end": v(25.9, -116) * mm});
            skLineSegment(sketch, "E96.12.11.0", {"start": v(25.9, -116) * mm, "end": v(25.9, -121) * mm});
            skLineSegment(sketch, "E96.15.11.0", {"start": v(26.9, -117) * mm, "end": v(26.9, -120) * mm});
            skLineSegment(sketch, "E96.18.11.0", {"start": v(26.9, -120) * mm, "end": v(32.9, -120) * mm});
            skLineSegment(sketch, "E96.21.11.0", {"start": v(25.9, -121) * mm, "end": v(31.9, -121) * mm});
            skLineSegment(sketch, "E97.0", {"start": v(-25.9, 0) * mm, "end": v(-27.9, 0) * mm});
            skLineSegment(sketch, "E98.0.6.0", {"start": v(-32.8, -60.3) * mm, "end": v(-32.8, -65.1) * mm});
            skLineSegment(sketch, "E98.3.6.0", {"start": v(-31.8, -61.3) * mm, "end": v(-31.8, -64.1) * mm});
            skLineSegment(sketch, "E98.6.6.0", {"start": v(-31.8, -64.1) * mm, "end": v(-25.8, -64.1) * mm});
            skLineSegment(sketch, "E98.9.6.0", {"start": v(-32.8, -65.1) * mm, "end": v(-26.8, -65.1) * mm});
            skLineSegment(sketch, "E98.12.6.0", {"start": v(-25.8, -64.1) * mm, "end": v(-25.8, -71.35) * mm});
            skLineSegment(sketch, "E98.15.6.0", {"start": v(-26.8, -65.1) * mm, "end": v(-26.8, -70.35) * mm});
            skLineSegment(sketch, "E98.18.6.0", {"start": v(-26.8, -70.35) * mm, "end": v(-32.8, -70.35) * mm});
            skLineSegment(sketch, "E98.21.6.0", {"start": v(-25.8, -71.35) * mm, "end": v(-31.8, -71.35) * mm});
            skLineSegment(sketch, "E99", {"start": v(32.9, -120) * mm, "end": v(32.9, -121) * mm});
            skLineSegment(sketch, "E100", {"start": v(32.9, -121) * mm, "end": v(31.9, -121) * mm});
            skLineSegment(sketch, "E101", {"start": v(-31.8, -71.35) * mm, "end": v(-32.8, -71.35) * mm});
            skLineSegment(sketch, "E102", {"start": v(-32.8, -71.35) * mm, "end": v(-32.8, -70.35) * mm});
            skSolve(sketch);
        }
        {
            var Q0;
            Q0 = qSketchRegion(id + "F29", true);
            var Q1;
            Q1=makeQuery(id+"F22.opExtrude","CAP_FACE",FACE,{"disambiguationData":[OSD([sQuery(id+"F21.wireOp",EDGE,"E51.0"),sQuery(id+"F21.wireOp",EDGE,"E52.0"),sQuery(id+"F21.wireOp",EDGE,"E53.0"),sQuery(id+"F21.wireOp",EDGE,"E54.0"),sQuery(id+"F21.wireOp",EDGE,"E55.0"),sQuery(id+"F21.wireOp",EDGE,"E56"),sQuery(id+"F21.wireOp",EDGE,"E57"),sQuery(id+"F21.wireOp",EDGE,"E58"),sQuery(id+"F21.wireOp",EDGE,"E59.0"),sQuery(id+"F21.wireOp",EDGE,"E59.1"),sQuery(id+"F21.wireOp",EDGE,"E59.2"),sQuery(id+"F21.wireOp",EDGE,"E59.3"),sQuery(id+"F21.wireOp",EDGE,"E59.4"),sQuery(id+"F21.wireOp",EDGE,"E59.5"),sQuery(id+"F21.wireOp",EDGE,"E59.6"),sQuery(id+"F21.wireOp",EDGE,"E60")])],"isStart":false});
            extrude(context, id + "F30", {"entities" : qUnion([Q0]), "operationType" : NewBodyOperationType.ADD, "endBound" : BoundingType.UP_TO_SURFACE, "oppositeDirection" : true, "depth" : 25 * mm, "endBoundEntityFace" : qUnion([Q1]), "offsetDistance" : 25 * mm});
        }
        {
            var Q0;
            Q0=makeQuery(id+"F30.boolean.opBoolean","MERGE",FACE,{"derivedFrom":[makeQuery(id+"F22.opExtrude","CAP_FACE",FACE,{"disambiguationData":[OSD([sQuery(id+"F21.wireOp",EDGE,"E51.0"),sQuery(id+"F21.wireOp",EDGE,"E52.0"),sQuery(id+"F21.wireOp",EDGE,"E53.0"),sQuery(id+"F21.wireOp",EDGE,"E54.0"),sQuery(id+"F21.wireOp",EDGE,"E55.0"),sQuery(id+"F21.wireOp",EDGE,"E56"),sQuery(id+"F21.wireOp",EDGE,"E57"),sQuery(id+"F21.wireOp",EDGE,"E58"),sQuery(id+"F21.wireOp",EDGE,"E59.0"),sQuery(id+"F21.wireOp",EDGE,"E59.1"),sQuery(id+"F21.wireOp",EDGE,"E59.2"),sQuery(id+"F21.wireOp",EDGE,"E59.3"),sQuery(id+"F21.wireOp",EDGE,"E59.4"),sQuery(id+"F21.wireOp",EDGE,"E59.5"),sQuery(id+"F21.wireOp",EDGE,"E59.6"),sQuery(id+"F21.wireOp",EDGE,"E60")])],"isStart":true}),makeQuery(id+"F30.opExtrude","CAP_FACE",FACE,{"disambiguationData":[OSD([sQuery(id+"F29.wireOp",EDGE,"E67.0"),sQuery(id+"F29.wireOp",EDGE,"E68"),sQuery(id+"F29.wireOp",EDGE,"RktKdMTx-d1wt-ufl3-Xxl2-rdMHNRnhUrT1"),sQuery(id+"F29.wireOp",EDGE,"WBuemFVi-fMIH-R8t4-Qq3e-FEkwOaVznJNM"),sQuery(id+"F29.wireOp",EDGE,"dIZbrFCx-AWuh-ymnm-7fbJ-zZgMrCerckaN"),sQuery(id+"F29.wireOp",EDGE,"E69"),sQuery(id+"F29.wireOp",EDGE,"E70"),sQuery(id+"F29.wireOp",EDGE,"6ai2BQuS-oy0q-UA7c-mrVg-G2IHXEmEPLTP"),sQuery(id+"F29.wireOp",EDGE,"1ZXhm1K8-iyBW-BSkS-IjLN-yGtyT5ByQ1Mg"),sQuery(id+"F29.wireOp",EDGE,"avt1LHLu-5JcH-gQnm-WnDp-U2Gk57naUvDa"),sQuery(id+"F29.wireOp",EDGE,"c60bda9e-0676-484f-b727-77bd6d5c0cd1.1.0.0"),sQuery(id+"F29.wireOp",EDGE,"c60bda9e-0676-484f-b727-77bd6d5c0cd1.1.0.1"),sQuery(id+"F29.wireOp",EDGE,"c60bda9e-0676-484f-b727-77bd6d5c0cd1.1.0.2"),sQuery(id+"F29.wireOp",EDGE,"c60bda9e-0676-484f-b727-77bd6d5c0cd1.1.0.3"),sQuery(id+"F29.wireOp",EDGE,"c60bda9e-0676-484f-b727-77bd6d5c0cd1.1.0.4"),sQuery(id+"F29.wireOp",EDGE,"c60bda9e-0676-484f-b727-77bd6d5c0cd1.1.0.5"),sQuery(id+"F29.wireOp",EDGE,"c60bda9e-0676-484f-b727-77bd6d5c0cd1.1.0.6"),sQuery(id+"F29.wireOp",EDGE,"c60bda9e-0676-484f-b727-77bd6d5c0cd1.1.0.7"),sQuery(id+"F29.wireOp",EDGE,"c60bda9e-0676-484f-b727-77bd6d5c0cd1.2.0.0"),sQuery(id+"F29.wireOp",EDGE,"c60bda9e-0676-484f-b727-77bd6d5c0cd1.2.0.1"),sQuery(id+"F29.wireOp",EDGE,"c60bda9e-0676-484f-b727-77bd6d5c0cd1.2.0.2"),sQuery(id+"F29.wireOp",EDGE,"c60bda9e-0676-484f-b727-77bd6d5c0cd1.2.0.3"),sQuery(id+"F29.wireOp",EDGE,"c60bda9e-0676-484f-b727-77bd6d5c0cd1.2.0.4"),sQuery(id+"F29.wireOp",EDGE,"c60bda9e-0676-484f-b727-77bd6d5c0cd1.2.0.5"),sQuery(id+"F29.wireOp",EDGE,"c60bda9e-0676-484f-b727-77bd6d5c0cd1.2.0.6"),sQuery(id+"F29.wireOp",EDGE,"c60bda9e-0676-484f-b727-77bd6d5c0cd1.2.0.7"),sQuery(id+"F29.wireOp",EDGE,"c60bda9e-0676-484f-b727-77bd6d5c0cd1.3.0.0"),sQuery(id+"F29.wireOp",EDGE,"c60bda9e-0676-484f-b727-77bd6d5c0cd1.3.0.1"),sQuery(id+"F29.wireOp",EDGE,"c60bda9e-0676-484f-b727-77bd6d5c0cd1.3.0.2"),sQuery(id+"F29.wireOp",EDGE,"c60bda9e-0676-484f-b727-77bd6d5c0cd1.3.0.3"),sQuery(id+"F29.wireOp",EDGE,"c60bda9e-0676-484f-b727-77bd6d5c0cd1.3.0.4"),sQuery(id+"F29.wireOp",EDGE,"c60bda9e-0676-484f-b727-77bd6d5c0cd1.3.0.5"),sQuery(id+"F29.wireOp",EDGE,"c60bda9e-0676-484f-b727-77bd6d5c0cd1.3.0.6"),sQuery(id+"F29.wireOp",EDGE,"c60bda9e-0676-484f-b727-77bd6d5c0cd1.3.0.7"),sQuery(id+"F29.wireOp",EDGE,"c60bda9e-0676-484f-b727-77bd6d5c0cd1.4.0.0"),sQuery(id+"F29.wireOp",EDGE,"c60bda9e-0676-484f-b727-77bd6d5c0cd1.4.0.1"),sQuery(id+"F29.wireOp",EDGE,"c60bda9e-0676-484f-b727-77bd6d5c0cd1.4.0.2"),sQuery(id+"F29.wireOp",EDGE,"c60bda9e-0676-484f-b727-77bd6d5c0cd1.4.0.3"),sQuery(id+"F29.wireOp",EDGE,"c60bda9e-0676-484f-b727-77bd6d5c0cd1.4.0.4"),sQuery(id+"F29.wireOp",EDGE,"c60bda9e-0676-484f-b727-77bd6d5c0cd1.4.0.5"),sQuery(id+"F29.wireOp",EDGE,"c60bda9e-0676-484f-b727-77bd6d5c0cd1.4.0.6"),sQuery(id+"F29.wireOp",EDGE,"c60bda9e-0676-484f-b727-77bd6d5c0cd1.4.0.7"),sQuery(id+"F29.wireOp",EDGE,"c60bda9e-0676-484f-b727-77bd6d5c0cd1.5.0.0"),sQuery(id+"F29.wireOp",EDGE,"c60bda9e-0676-484f-b727-77bd6d5c0cd1.5.0.1"),sQuery(id+"F29.wireOp",EDGE,"c60bda9e-0676-484f-b727-77bd6d5c0cd1.5.0.2"),sQuery(id+"F29.wireOp",EDGE,"c60bda9e-0676-484f-b727-77bd6d5c0cd1.5.0.3"),sQuery(id+"F29.wireOp",EDGE,"c60bda9e-0676-484f-b727-77bd6d5c0cd1.5.0.4"),sQuery(id+"F29.wireOp",EDGE,"c60bda9e-0676-484f-b727-77bd6d5c0cd1.5.0.5"),sQuery(id+"F29.wireOp",EDGE,"c60bda9e-0676-484f-b727-77bd6d5c0cd1.5.0.6"),sQuery(id+"F29.wireOp",EDGE,"c60bda9e-0676-484f-b727-77bd6d5c0cd1.5.0.7"),sQuery(id+"F29.wireOp",EDGE,"c60bda9e-0676-484f-b727-77bd6d5c0cd1.6.0.0"),sQuery(id+"F29.wireOp",EDGE,"c60bda9e-0676-484f-b727-77bd6d5c0cd1.6.0.1"),sQuery(id+"F29.wireOp",EDGE,"c60bda9e-0676-484f-b727-77bd6d5c0cd1.6.0.2"),sQuery(id+"F29.wireOp",EDGE,"c60bda9e-0676-484f-b727-77bd6d5c0cd1.6.0.3"),sQuery(id+"F29.wireOp",EDGE,"c60bda9e-0676-484f-b727-77bd6d5c0cd1.6.0.4"),sQuery(id+"F29.wireOp",EDGE,"c60bda9e-0676-484f-b727-77bd6d5c0cd1.6.0.5"),sQuery(id+"F29.wireOp",EDGE,"c60bda9e-0676-484f-b727-77bd6d5c0cd1.6.0.6"),sQuery(id+"F29.wireOp",EDGE,"c60bda9e-0676-484f-b727-77bd6d5c0cd1.6.0.7"),sQuery(id+"F29.wireOp",EDGE,"k0yNZAr2-dlr9-qzV1-gzhJ-MxstemT8P6j7"),sQuery(id+"F29.wireOp",EDGE,"g8fHv0zq-H3ls-mroi-CYxu-16rIa7HBAOaZ")])],"isStart":true}),makeQuery(id+"F30.opExtrude","CAP_FACE",FACE,{"disambiguationData":[OSD([sQuery(id+"F29.wireOp",EDGE,"bd187669-9fd1-4d3a-ba9d-e1158454d08e.0"),sQuery(id+"F29.wireOp",EDGE,"tj3evFk7-oHeL-tKLx-QfEg-dtW89470cT6I"),sQuery(id+"F29.wireOp",EDGE,"UMJX5k7Y-g80L-6GNA-aDj0-d1GjIul9mRqf"),sQuery(id+"F29.wireOp",EDGE,"oyEF6hgW-HFwy-Fenx-keWR-uhUsMn79rERw"),sQuery(id+"F29.wireOp",EDGE,"UWuyJX2g-uRi5-GRQ7-956j-zVijAR0075Nw"),sQuery(id+"F29.wireOp",EDGE,"dpX4U3Td-E2bf-75GA-BHam-uyOve8EahZDj"),sQuery(id+"F29.wireOp",EDGE,"vLAoP9MU-sN8v-dXyB-76jy-QzkbcWfSWZsG"),sQuery(id+"F29.wireOp",EDGE,"RAxh2FcG-smY4-6XsJ-6Qed-H3qQyYCBnOkD"),sQuery(id+"F29.wireOp",EDGE,"qk3SouKL-6OS9-riTA-71iJ-Kddj04mNiint"),sQuery(id+"F29.wireOp",EDGE,"xeKQrIuv-15MR-j1wm-sDkC-XsrgeaC8G8d3"),sQuery(id+"F29.wireOp",EDGE,"fe6c96f3-bb83-408c-b3be-38af7d7b5ba0.1.0.0"),sQuery(id+"F29.wireOp",EDGE,"fe6c96f3-bb83-408c-b3be-38af7d7b5ba0.1.0.1"),sQuery(id+"F29.wireOp",EDGE,"fe6c96f3-bb83-408c-b3be-38af7d7b5ba0.1.0.2"),sQuery(id+"F29.wireOp",EDGE,"fe6c96f3-bb83-408c-b3be-38af7d7b5ba0.1.0.3"),sQuery(id+"F29.wireOp",EDGE,"fe6c96f3-bb83-408c-b3be-38af7d7b5ba0.1.0.4"),sQuery(id+"F29.wireOp",EDGE,"fe6c96f3-bb83-408c-b3be-38af7d7b5ba0.1.0.5"),sQuery(id+"F29.wireOp",EDGE,"fe6c96f3-bb83-408c-b3be-38af7d7b5ba0.1.0.6"),sQuery(id+"F29.wireOp",EDGE,"fe6c96f3-bb83-408c-b3be-38af7d7b5ba0.1.0.7"),sQuery(id+"F29.wireOp",EDGE,"fe6c96f3-bb83-408c-b3be-38af7d7b5ba0.2.0.0"),sQuery(id+"F29.wireOp",EDGE,"fe6c96f3-bb83-408c-b3be-38af7d7b5ba0.2.0.1"),sQuery(id+"F29.wireOp",EDGE,"fe6c96f3-bb83-408c-b3be-38af7d7b5ba0.2.0.2"),sQuery(id+"F29.wireOp",EDGE,"fe6c96f3-bb83-408c-b3be-38af7d7b5ba0.2.0.3"),sQuery(id+"F29.wireOp",EDGE,"fe6c96f3-bb83-408c-b3be-38af7d7b5ba0.2.0.4"),sQuery(id+"F29.wireOp",EDGE,"fe6c96f3-bb83-408c-b3be-38af7d7b5ba0.2.0.5"),sQuery(id+"F29.wireOp",EDGE,"fe6c96f3-bb83-408c-b3be-38af7d7b5ba0.2.0.6"),sQuery(id+"F29.wireOp",EDGE,"fe6c96f3-bb83-408c-b3be-38af7d7b5ba0.2.0.7"),sQuery(id+"F29.wireOp",EDGE,"5d80d0a8-d5f9-4584-8569-0b86ccec6197.0.3.0"),sQuery(id+"F29.wireOp",EDGE,"5d80d0a8-d5f9-4584-8569-0b86ccec6197.3.3.0"),sQuery(id+"F29.wireOp",EDGE,"5d80d0a8-d5f9-4584-8569-0b86ccec6197.6.3.0"),sQuery(id+"F29.wireOp",EDGE,"5d80d0a8-d5f9-4584-8569-0b86ccec6197.9.3.0"),sQuery(id+"F29.wireOp",EDGE,"5d80d0a8-d5f9-4584-8569-0b86ccec6197.12.3.0"),sQuery(id+"F29.wireOp",EDGE,"5d80d0a8-d5f9-4584-8569-0b86ccec6197.15.3.0"),sQuery(id+"F29.wireOp",EDGE,"5d80d0a8-d5f9-4584-8569-0b86ccec6197.18.3.0"),sQuery(id+"F29.wireOp",EDGE,"5d80d0a8-d5f9-4584-8569-0b86ccec6197.21.3.0"),sQuery(id+"F29.wireOp",EDGE,"1rMCYFLr-05Lj-RyTw-BCct-ELeWgdjBYhRu"),sQuery(id+"F29.wireOp",EDGE,"p1nw8Oho-PIP2-emn9-eYmt-nff5l7aM6hfX")])],"isStart":true})]});
            var sketch = newSketch(context, id + "F31", { "sketchPlane" : qUnion([Q0])});
            skLineSegment(sketch, "E103.bottom", {"start": v(-25.8, -61.3) * mm, "end": v(-37.8, -61.3) * mm});
            skLineSegment(sketch, "E103.top", {"start": v(-25.8, -40.2) * mm, "end": v(-37.8, -40.2) * mm});
            skLineSegment(sketch, "E103.left", {"start": v(-25.8, -61.3) * mm, "end": v(-25.8, -40.2) * mm});
            skLineSegment(sketch, "E103.right", {"start": v(-37.8, -61.3) * mm, "end": v(-37.8, -40.2) * mm});
            skPoint(sketch, "E104.0", {"position": v(-25.8, -61.3) * mm});
            skSolve(sketch);
        }
        {
            var Q0;
            Q0=makeQuery(id+"F30.boolean.opBoolean","MERGE",FACE,{"derivedFrom":[makeQuery(id+"F22.opExtrude","CAP_FACE",FACE,{"disambiguationData":[OSD([sQuery(id+"F21.wireOp",EDGE,"E51.0"),sQuery(id+"F21.wireOp",EDGE,"E52.0"),sQuery(id+"F21.wireOp",EDGE,"E53.0"),sQuery(id+"F21.wireOp",EDGE,"E54.0"),sQuery(id+"F21.wireOp",EDGE,"E55.0"),sQuery(id+"F21.wireOp",EDGE,"E56"),sQuery(id+"F21.wireOp",EDGE,"E57"),sQuery(id+"F21.wireOp",EDGE,"E58"),sQuery(id+"F21.wireOp",EDGE,"E59.0"),sQuery(id+"F21.wireOp",EDGE,"E59.1"),sQuery(id+"F21.wireOp",EDGE,"E59.2"),sQuery(id+"F21.wireOp",EDGE,"E59.3"),sQuery(id+"F21.wireOp",EDGE,"E59.4"),sQuery(id+"F21.wireOp",EDGE,"E59.5"),sQuery(id+"F21.wireOp",EDGE,"E59.6"),sQuery(id+"F21.wireOp",EDGE,"E60")])],"isStart":false}),makeQuery(id+"F30.opExtrude","CAP_FACE",FACE,{"disambiguationData":[OSD([sQuery(id+"F29.wireOp",EDGE,"E67.0"),sQuery(id+"F29.wireOp",EDGE,"E68"),sQuery(id+"F29.wireOp",EDGE,"RktKdMTx-d1wt-ufl3-Xxl2-rdMHNRnhUrT1"),sQuery(id+"F29.wireOp",EDGE,"WBuemFVi-fMIH-R8t4-Qq3e-FEkwOaVznJNM"),sQuery(id+"F29.wireOp",EDGE,"dIZbrFCx-AWuh-ymnm-7fbJ-zZgMrCerckaN"),sQuery(id+"F29.wireOp",EDGE,"E69"),sQuery(id+"F29.wireOp",EDGE,"E70"),sQuery(id+"F29.wireOp",EDGE,"6ai2BQuS-oy0q-UA7c-mrVg-G2IHXEmEPLTP"),sQuery(id+"F29.wireOp",EDGE,"1ZXhm1K8-iyBW-BSkS-IjLN-yGtyT5ByQ1Mg"),sQuery(id+"F29.wireOp",EDGE,"avt1LHLu-5JcH-gQnm-WnDp-U2Gk57naUvDa"),sQuery(id+"F29.wireOp",EDGE,"c60bda9e-0676-484f-b727-77bd6d5c0cd1.1.0.0"),sQuery(id+"F29.wireOp",EDGE,"c60bda9e-0676-484f-b727-77bd6d5c0cd1.1.0.1"),sQuery(id+"F29.wireOp",EDGE,"c60bda9e-0676-484f-b727-77bd6d5c0cd1.1.0.2"),sQuery(id+"F29.wireOp",EDGE,"c60bda9e-0676-484f-b727-77bd6d5c0cd1.1.0.3"),sQuery(id+"F29.wireOp",EDGE,"c60bda9e-0676-484f-b727-77bd6d5c0cd1.1.0.4"),sQuery(id+"F29.wireOp",EDGE,"c60bda9e-0676-484f-b727-77bd6d5c0cd1.1.0.5"),sQuery(id+"F29.wireOp",EDGE,"c60bda9e-0676-484f-b727-77bd6d5c0cd1.1.0.6"),sQuery(id+"F29.wireOp",EDGE,"c60bda9e-0676-484f-b727-77bd6d5c0cd1.1.0.7"),sQuery(id+"F29.wireOp",EDGE,"c60bda9e-0676-484f-b727-77bd6d5c0cd1.2.0.0"),sQuery(id+"F29.wireOp",EDGE,"c60bda9e-0676-484f-b727-77bd6d5c0cd1.2.0.1"),sQuery(id+"F29.wireOp",EDGE,"c60bda9e-0676-484f-b727-77bd6d5c0cd1.2.0.2"),sQuery(id+"F29.wireOp",EDGE,"c60bda9e-0676-484f-b727-77bd6d5c0cd1.2.0.3"),sQuery(id+"F29.wireOp",EDGE,"c60bda9e-0676-484f-b727-77bd6d5c0cd1.2.0.4"),sQuery(id+"F29.wireOp",EDGE,"c60bda9e-0676-484f-b727-77bd6d5c0cd1.2.0.5"),sQuery(id+"F29.wireOp",EDGE,"c60bda9e-0676-484f-b727-77bd6d5c0cd1.2.0.6"),sQuery(id+"F29.wireOp",EDGE,"c60bda9e-0676-484f-b727-77bd6d5c0cd1.2.0.7"),sQuery(id+"F29.wireOp",EDGE,"c60bda9e-0676-484f-b727-77bd6d5c0cd1.3.0.0"),sQuery(id+"F29.wireOp",EDGE,"c60bda9e-0676-484f-b727-77bd6d5c0cd1.3.0.1"),sQuery(id+"F29.wireOp",EDGE,"c60bda9e-0676-484f-b727-77bd6d5c0cd1.3.0.2"),sQuery(id+"F29.wireOp",EDGE,"c60bda9e-0676-484f-b727-77bd6d5c0cd1.3.0.3"),sQuery(id+"F29.wireOp",EDGE,"c60bda9e-0676-484f-b727-77bd6d5c0cd1.3.0.4"),sQuery(id+"F29.wireOp",EDGE,"c60bda9e-0676-484f-b727-77bd6d5c0cd1.3.0.5"),sQuery(id+"F29.wireOp",EDGE,"c60bda9e-0676-484f-b727-77bd6d5c0cd1.3.0.6"),sQuery(id+"F29.wireOp",EDGE,"c60bda9e-0676-484f-b727-77bd6d5c0cd1.3.0.7"),sQuery(id+"F29.wireOp",EDGE,"c60bda9e-0676-484f-b727-77bd6d5c0cd1.4.0.0"),sQuery(id+"F29.wireOp",EDGE,"c60bda9e-0676-484f-b727-77bd6d5c0cd1.4.0.1"),sQuery(id+"F29.wireOp",EDGE,"c60bda9e-0676-484f-b727-77bd6d5c0cd1.4.0.2"),sQuery(id+"F29.wireOp",EDGE,"c60bda9e-0676-484f-b727-77bd6d5c0cd1.4.0.3"),sQuery(id+"F29.wireOp",EDGE,"c60bda9e-0676-484f-b727-77bd6d5c0cd1.4.0.4"),sQuery(id+"F29.wireOp",EDGE,"c60bda9e-0676-484f-b727-77bd6d5c0cd1.4.0.5"),sQuery(id+"F29.wireOp",EDGE,"c60bda9e-0676-484f-b727-77bd6d5c0cd1.4.0.6"),sQuery(id+"F29.wireOp",EDGE,"c60bda9e-0676-484f-b727-77bd6d5c0cd1.4.0.7"),sQuery(id+"F29.wireOp",EDGE,"c60bda9e-0676-484f-b727-77bd6d5c0cd1.5.0.0"),sQuery(id+"F29.wireOp",EDGE,"c60bda9e-0676-484f-b727-77bd6d5c0cd1.5.0.1"),sQuery(id+"F29.wireOp",EDGE,"c60bda9e-0676-484f-b727-77bd6d5c0cd1.5.0.2"),sQuery(id+"F29.wireOp",EDGE,"c60bda9e-0676-484f-b727-77bd6d5c0cd1.5.0.3"),sQuery(id+"F29.wireOp",EDGE,"c60bda9e-0676-484f-b727-77bd6d5c0cd1.5.0.4"),sQuery(id+"F29.wireOp",EDGE,"c60bda9e-0676-484f-b727-77bd6d5c0cd1.5.0.5"),sQuery(id+"F29.wireOp",EDGE,"c60bda9e-0676-484f-b727-77bd6d5c0cd1.5.0.6"),sQuery(id+"F29.wireOp",EDGE,"c60bda9e-0676-484f-b727-77bd6d5c0cd1.5.0.7"),sQuery(id+"F29.wireOp",EDGE,"c60bda9e-0676-484f-b727-77bd6d5c0cd1.6.0.0"),sQuery(id+"F29.wireOp",EDGE,"c60bda9e-0676-484f-b727-77bd6d5c0cd1.6.0.1"),sQuery(id+"F29.wireOp",EDGE,"c60bda9e-0676-484f-b727-77bd6d5c0cd1.6.0.2"),sQuery(id+"F29.wireOp",EDGE,"c60bda9e-0676-484f-b727-77bd6d5c0cd1.6.0.3"),sQuery(id+"F29.wireOp",EDGE,"c60bda9e-0676-484f-b727-77bd6d5c0cd1.6.0.4"),sQuery(id+"F29.wireOp",EDGE,"c60bda9e-0676-484f-b727-77bd6d5c0cd1.6.0.5"),sQuery(id+"F29.wireOp",EDGE,"c60bda9e-0676-484f-b727-77bd6d5c0cd1.6.0.6"),sQuery(id+"F29.wireOp",EDGE,"c60bda9e-0676-484f-b727-77bd6d5c0cd1.6.0.7"),sQuery(id+"F29.wireOp",EDGE,"k0yNZAr2-dlr9-qzV1-gzhJ-MxstemT8P6j7"),sQuery(id+"F29.wireOp",EDGE,"g8fHv0zq-H3ls-mroi-CYxu-16rIa7HBAOaZ")])],"isStart":false}),makeQuery(id+"F30.opExtrude","CAP_FACE",FACE,{"disambiguationData":[OSD([sQuery(id+"F29.wireOp",EDGE,"bd187669-9fd1-4d3a-ba9d-e1158454d08e.0"),sQuery(id+"F29.wireOp",EDGE,"tj3evFk7-oHeL-tKLx-QfEg-dtW89470cT6I"),sQuery(id+"F29.wireOp",EDGE,"UMJX5k7Y-g80L-6GNA-aDj0-d1GjIul9mRqf"),sQuery(id+"F29.wireOp",EDGE,"oyEF6hgW-HFwy-Fenx-keWR-uhUsMn79rERw"),sQuery(id+"F29.wireOp",EDGE,"UWuyJX2g-uRi5-GRQ7-956j-zVijAR0075Nw"),sQuery(id+"F29.wireOp",EDGE,"dpX4U3Td-E2bf-75GA-BHam-uyOve8EahZDj"),sQuery(id+"F29.wireOp",EDGE,"vLAoP9MU-sN8v-dXyB-76jy-QzkbcWfSWZsG"),sQuery(id+"F29.wireOp",EDGE,"RAxh2FcG-smY4-6XsJ-6Qed-H3qQyYCBnOkD"),sQuery(id+"F29.wireOp",EDGE,"qk3SouKL-6OS9-riTA-71iJ-Kddj04mNiint"),sQuery(id+"F29.wireOp",EDGE,"xeKQrIuv-15MR-j1wm-sDkC-XsrgeaC8G8d3"),sQuery(id+"F29.wireOp",EDGE,"fe6c96f3-bb83-408c-b3be-38af7d7b5ba0.1.0.0"),sQuery(id+"F29.wireOp",EDGE,"fe6c96f3-bb83-408c-b3be-38af7d7b5ba0.1.0.1"),sQuery(id+"F29.wireOp",EDGE,"fe6c96f3-bb83-408c-b3be-38af7d7b5ba0.1.0.2"),sQuery(id+"F29.wireOp",EDGE,"fe6c96f3-bb83-408c-b3be-38af7d7b5ba0.1.0.3"),sQuery(id+"F29.wireOp",EDGE,"fe6c96f3-bb83-408c-b3be-38af7d7b5ba0.1.0.4"),sQuery(id+"F29.wireOp",EDGE,"fe6c96f3-bb83-408c-b3be-38af7d7b5ba0.1.0.5"),sQuery(id+"F29.wireOp",EDGE,"fe6c96f3-bb83-408c-b3be-38af7d7b5ba0.1.0.6"),sQuery(id+"F29.wireOp",EDGE,"fe6c96f3-bb83-408c-b3be-38af7d7b5ba0.1.0.7"),sQuery(id+"F29.wireOp",EDGE,"fe6c96f3-bb83-408c-b3be-38af7d7b5ba0.2.0.0"),sQuery(id+"F29.wireOp",EDGE,"fe6c96f3-bb83-408c-b3be-38af7d7b5ba0.2.0.1"),sQuery(id+"F29.wireOp",EDGE,"fe6c96f3-bb83-408c-b3be-38af7d7b5ba0.2.0.2"),sQuery(id+"F29.wireOp",EDGE,"fe6c96f3-bb83-408c-b3be-38af7d7b5ba0.2.0.3"),sQuery(id+"F29.wireOp",EDGE,"fe6c96f3-bb83-408c-b3be-38af7d7b5ba0.2.0.4"),sQuery(id+"F29.wireOp",EDGE,"fe6c96f3-bb83-408c-b3be-38af7d7b5ba0.2.0.5"),sQuery(id+"F29.wireOp",EDGE,"fe6c96f3-bb83-408c-b3be-38af7d7b5ba0.2.0.6"),sQuery(id+"F29.wireOp",EDGE,"fe6c96f3-bb83-408c-b3be-38af7d7b5ba0.2.0.7"),sQuery(id+"F29.wireOp",EDGE,"5d80d0a8-d5f9-4584-8569-0b86ccec6197.0.3.0"),sQuery(id+"F29.wireOp",EDGE,"5d80d0a8-d5f9-4584-8569-0b86ccec6197.3.3.0"),sQuery(id+"F29.wireOp",EDGE,"5d80d0a8-d5f9-4584-8569-0b86ccec6197.6.3.0"),sQuery(id+"F29.wireOp",EDGE,"5d80d0a8-d5f9-4584-8569-0b86ccec6197.9.3.0"),sQuery(id+"F29.wireOp",EDGE,"5d80d0a8-d5f9-4584-8569-0b86ccec6197.12.3.0"),sQuery(id+"F29.wireOp",EDGE,"5d80d0a8-d5f9-4584-8569-0b86ccec6197.15.3.0"),sQuery(id+"F29.wireOp",EDGE,"5d80d0a8-d5f9-4584-8569-0b86ccec6197.18.3.0"),sQuery(id+"F29.wireOp",EDGE,"5d80d0a8-d5f9-4584-8569-0b86ccec6197.21.3.0"),sQuery(id+"F29.wireOp",EDGE,"1rMCYFLr-05Lj-RyTw-BCct-ELeWgdjBYhRu"),sQuery(id+"F29.wireOp",EDGE,"p1nw8Oho-PIP2-emn9-eYmt-nff5l7aM6hfX")])],"isStart":false})]});
            var sketch = newSketch(context, id + "F32", { "sketchPlane" : qUnion([Q0])});
            skLineSegment(sketch, "E105.bottom", {"start": v(25.9, -58) * mm, "end": v(25.9, -58) * mm});
            skLineSegment(sketch, "E105.top", {"start": v(25.9, -33) * mm, "end": v(25.9, -33) * mm});
            skLineSegment(sketch, "E105.left", {"start": v(25.9, -58) * mm, "end": v(25.9, -33) * mm});
            skLineSegment(sketch, "E105.right", {"start": v(25.9, -58) * mm, "end": v(25.9, -33) * mm});
            skSolve(sketch);
        }
        {
            var Q0;
            Q0=makeQuery(id+"F22.opExtrude","SWEPT_FACE",FACE,{"disambiguationData":[OSD([sQuery(id+"F21.wireOp",EDGE,"E59.6")])]});
            var sketch = newSketch(context, id + "F33", { "sketchPlane" : qUnion([Q0])});
            skCircle(sketch, "E106.0", {"center": v(2.1, 0.1) * mm, "radius": 2.5 * mm});
            skSolve(sketch);
        }
        {
            var Q0;
            Q0 = qSketchRegion(id + "F33", true);
            extrude(context, id + "F34", {"entities" : qUnion([Q0]), "operationType" : NewBodyOperationType.REMOVE, "endBound" : BoundingType.UP_TO_NEXT, "oppositeDirection" : true, "depth" : 25 * mm, "offsetDistance" : 25 * mm});
        }
        {
            var Q0;
            {var subQ1=sQuery(id+"F13.wireOp",EDGE,"E30");var subQ2=sQuery(id+"F13.wireOp",EDGE,"E32.MirrorCS");var subQ3=sQuery(id+"F13.wireOp",EDGE,"E31");Q0=makeQuery(id+"F28.boolean.opBoolean","SPLIT",FACE,{"disambiguationData":[TD([makeQuery(id+"F15.opShell","OFFSET_FACE",FACE,{"disambiguationData":[OSD([subQ1])]})])],"derivedFrom":makeQuery(id+"F15.opShell","OFFSET_FACE",FACE,{"disambiguationData":[OSD([subQ3,subQ2])]})});}
            var sketch = newSketch(context, id + "F35", { "sketchPlane" : qUnion([Q0])});
            skCircle(sketch, "E107.0", {"center": v(2.1, -0.1) * mm, "radius": 4.75 * mm});
            skSolve(sketch);
        }
        {
            var Q0;
            Q0 = qSketchRegion(id + "F35", true);
            extrude(context, id + "F36", {"entities" : qUnion([Q0]), "depth" : 3.5 * mm, "offsetDistance" : 25 * mm});
        }
        {
            var Q0;
            Q0=makeQuery(id+"F36.opExtrude","CAP_FACE",FACE,{"disambiguationData":[OSD([sQuery(id+"F35.wireOp",EDGE,"E107.0")])],"isStart":true});
            var sketch = newSketch(context, id + "F37", { "sketchPlane" : qUnion([Q0])});
            skCircle(sketch, "E108.0", {"center": v(2.1, 0.1) * mm, "radius": 2.25 * mm});
            skSolve(sketch);
        }
        {
            var Q0;
            Q0 = qSketchRegion(id + "F37", true);
            extrude(context, id + "F38", {"entities" : qUnion([Q0]), "operationType" : NewBodyOperationType.ADD, "depth" : 5 * mm, "offsetDistance" : 25 * mm});
        }
        {
            var Q0;
            Q0=makeQuery(id+"F38.opExtrude","CAP_EDGE",EDGE,{"disambiguationData":[OSD([sQuery(id+"F37.wireOp",EDGE,"E108.0")])],"isStart":false});
            fillet(context, id + "F39", {"entities" : qUnion([Q0]), "radius" : 1 * mm, "tangentPropagation" : true, "allowEdgeOverflow" : false});
        }
        {
            var Q0;
            Q0=makeQuery(id+"F36.opExtrude","CAP_EDGE",EDGE,{"disambiguationData":[OSD([sQuery(id+"F35.wireOp",EDGE,"E107.0")])],"isStart":false});
            chamfer(context, id + "F40", {"entities" : qUnion([Q0]), "width" : 2 * mm, "tangentPropagation" : true});
        }
        {
            var Q0;
            {var subQ0=sQuery(id+"F31.wireOp",EDGE,"E103.bottom");var subQ1=sQuery(id+"F31.wireOp",EDGE,"E103.top");var subQ2=sQuery(id+"F31.wireOp",EDGE,"E103.right");Q0=makeQuery(id+"FVIhOER6PHQ3Ug9_4.boolean.opBoolean","SPLIT",FACE,{"disambiguationData":[TD([makeQuery(id+"F30.opExtrude","SWEPT_FACE",FACE,{"disambiguationData":[OSD([sQuery(id+"F29.wireOp",EDGE,"E95.18.3.0")])]})])],"derivedFrom":makeQuery(id+"FVIhOER6PHQ3Ug9_4.opExtrude","CAP_FACE",FACE,{"disambiguationData":[OSD([subQ0,subQ1,sQuery(id+"F31.wireOp",EDGE,"E103.left"),subQ2])],"isStart":true})});}
            var sketch = newSketch(context, id + "F41", { "sketchPlane" : qUnion([Q0])});
            skLineSegment(sketch, "E109.bottom", {"start": v(37.8, -61.3) * mm, "end": v(34.3, -61.3) * mm});
            skLineSegment(sketch, "E109.top", {"start": v(37.8, -40.2) * mm, "end": v(34.3, -40.2) * mm});
            skLineSegment(sketch, "E109.left", {"start": v(37.8, -61.3) * mm, "end": v(37.8, -40.2) * mm});
            skLineSegment(sketch, "E109.right", {"start": v(34.3, -61.3) * mm, "end": v(34.3, -40.2) * mm});
            skSolve(sketch);
        }
        {
            var Q0;
            Q0=makeQuery(id+"F32.imprint","IMPRINT",FACE,{"disambiguationData":[TD([[makeQuery(id+"F32.imprint","IMPRINT",EDGE,{"derivedFrom":makeQuery(id+"F22.opExtrude","CAP_EDGE",EDGE,{"disambiguationData":[OSD([sQuery(id+"F21.wireOp",EDGE,"E51.0")])],"isStart":false})}),-1.0]])]});
            var sketch = newSketch(context, id + "F42", { "sketchPlane" : qUnion([Q0])});
            skPoint(sketch, "E110.0", {"position": v(-25.9, -1) * mm});
            skLineSegment(sketch, "E111.bottom", {"start": v(-25.9, -1) * mm, "end": v(-23.9, -1) * mm});
            skLineSegment(sketch, "E111.top", {"start": v(-25.9, 0) * mm, "end": v(-23.9, 0) * mm});
            skLineSegment(sketch, "E111.left", {"start": v(-25.9, -1) * mm, "end": v(-25.9, 0) * mm});
            skLineSegment(sketch, "E111.right", {"start": v(-23.9, -1) * mm, "end": v(-23.9, 0) * mm});
            skLineSegment(sketch, "E112.MirrorCS", {"start": v(23.9, -1) * mm, "end": v(23.9, 0) * mm});
            skLineSegment(sketch, "E113.MirrorCS", {"start": v(25.9, -1) * mm, "end": v(25.9, 0) * mm});
            skLineSegment(sketch, "E114.MirrorCS", {"start": v(25.9, -1) * mm, "end": v(23.9, -1) * mm});
            skLineSegment(sketch, "E115.MirrorCS", {"start": v(25.9, 0) * mm, "end": v(23.9, 0) * mm});
            skPoint(sketch, "E116.MirrorP", {"position": v(25.9, -1) * mm});
            skSolve(sketch);
        }
        {
            var Q0;
            Q0 = qSketchRegion(id + "F42", true);
            var Q1;
            Q1=makeQuery(id+"F30.boolean.opBoolean","MERGE",FACE,{"derivedFrom":[makeQuery(id+"F22.opExtrude","CAP_FACE",FACE,{"disambiguationData":[OSD([sQuery(id+"F21.wireOp",EDGE,"E51.0"),sQuery(id+"F21.wireOp",EDGE,"E52.0"),sQuery(id+"F21.wireOp",EDGE,"E53.0"),sQuery(id+"F21.wireOp",EDGE,"E54.0"),sQuery(id+"F21.wireOp",EDGE,"E55.0"),sQuery(id+"F21.wireOp",EDGE,"E56"),sQuery(id+"F21.wireOp",EDGE,"E57"),sQuery(id+"F21.wireOp",EDGE,"E58"),sQuery(id+"F21.wireOp",EDGE,"E59.0"),sQuery(id+"F21.wireOp",EDGE,"E59.1"),sQuery(id+"F21.wireOp",EDGE,"E59.2"),sQuery(id+"F21.wireOp",EDGE,"E59.3"),sQuery(id+"F21.wireOp",EDGE,"E59.4"),sQuery(id+"F21.wireOp",EDGE,"E59.5"),sQuery(id+"F21.wireOp",EDGE,"E59.6"),sQuery(id+"F21.wireOp",EDGE,"E60")])],"isStart":true}),makeQuery(id+"F30.opExtrude","CAP_FACE",FACE,{"disambiguationData":[OSD([sQuery(id+"F29.wireOp",EDGE,"E67.0"),sQuery(id+"F29.wireOp",EDGE,"E68"),sQuery(id+"F29.wireOp",EDGE,"E69"),sQuery(id+"F29.wireOp",EDGE,"E70"),sQuery(id+"F29.wireOp",EDGE,"E71"),sQuery(id+"F29.wireOp",EDGE,"E72"),sQuery(id+"F29.wireOp",EDGE,"E73"),sQuery(id+"F29.wireOp",EDGE,"E74"),sQuery(id+"F29.wireOp",EDGE,"E75"),sQuery(id+"F29.wireOp",EDGE,"E76"),sQuery(id+"F29.wireOp",EDGE,"E77"),sQuery(id+"F29.wireOp",EDGE,"E78"),sQuery(id+"F29.wireOp",EDGE,"E79.1.0.0"),sQuery(id+"F29.wireOp",EDGE,"E79.1.0.1"),sQuery(id+"F29.wireOp",EDGE,"E79.1.0.2"),sQuery(id+"F29.wireOp",EDGE,"E79.1.0.3"),sQuery(id+"F29.wireOp",EDGE,"E79.1.0.4"),sQuery(id+"F29.wireOp",EDGE,"E79.1.0.5"),sQuery(id+"F29.wireOp",EDGE,"E79.1.0.6"),sQuery(id+"F29.wireOp",EDGE,"E79.1.0.7"),sQuery(id+"F29.wireOp",EDGE,"E79.2.0.0"),sQuery(id+"F29.wireOp",EDGE,"E79.2.0.1"),sQuery(id+"F29.wireOp",EDGE,"E79.2.0.2"),sQuery(id+"F29.wireOp",EDGE,"E79.2.0.3"),sQuery(id+"F29.wireOp",EDGE,"E79.2.0.4"),sQuery(id+"F29.wireOp",EDGE,"E79.2.0.5"),sQuery(id+"F29.wireOp",EDGE,"E79.2.0.6"),sQuery(id+"F29.wireOp",EDGE,"E79.2.0.7"),sQuery(id+"F29.wireOp",EDGE,"E80.0.3.0"),sQuery(id+"F29.wireOp",EDGE,"E80.3.3.0"),sQuery(id+"F29.wireOp",EDGE,"E80.6.3.0"),sQuery(id+"F29.wireOp",EDGE,"E80.9.3.0"),sQuery(id+"F29.wireOp",EDGE,"E80.12.3.0"),sQuery(id+"F29.wireOp",EDGE,"E80.15.3.0"),sQuery(id+"F29.wireOp",EDGE,"E80.18.3.0"),sQuery(id+"F29.wireOp",EDGE,"E80.21.3.0"),sQuery(id+"F29.wireOp",EDGE,"E80.0.4.0"),sQuery(id+"F29.wireOp",EDGE,"E80.3.4.0"),sQuery(id+"F29.wireOp",EDGE,"E80.6.4.0"),sQuery(id+"F29.wireOp",EDGE,"E80.9.4.0"),sQuery(id+"F29.wireOp",EDGE,"E80.12.4.0"),sQuery(id+"F29.wireOp",EDGE,"E80.15.4.0"),sQuery(id+"F29.wireOp",EDGE,"E80.18.4.0"),sQuery(id+"F29.wireOp",EDGE,"E80.21.4.0"),sQuery(id+"F29.wireOp",EDGE,"E80.0.5.0"),sQuery(id+"F29.wireOp",EDGE,"E80.3.5.0"),sQuery(id+"F29.wireOp",EDGE,"E80.6.5.0"),sQuery(id+"F29.wireOp",EDGE,"E80.9.5.0"),sQuery(id+"F29.wireOp",EDGE,"E80.12.5.0"),sQuery(id+"F29.wireOp",EDGE,"E80.15.5.0"),sQuery(id+"F29.wireOp",EDGE,"E80.18.5.0"),sQuery(id+"F29.wireOp",EDGE,"E80.21.5.0"),sQuery(id+"F29.wireOp",EDGE,"E80.0.6.0"),sQuery(id+"F29.wireOp",EDGE,"E80.3.6.0"),sQuery(id+"F29.wireOp",EDGE,"E80.6.6.0"),sQuery(id+"F29.wireOp",EDGE,"E80.9.6.0"),sQuery(id+"F29.wireOp",EDGE,"E80.12.6.0"),sQuery(id+"F29.wireOp",EDGE,"E80.15.6.0"),sQuery(id+"F29.wireOp",EDGE,"E80.18.6.0"),sQuery(id+"F29.wireOp",EDGE,"E80.21.6.0"),sQuery(id+"F29.wireOp",EDGE,"E80.0.7.0"),sQuery(id+"F29.wireOp",EDGE,"E80.3.7.0"),sQuery(id+"F29.wireOp",EDGE,"E80.6.7.0"),sQuery(id+"F29.wireOp",EDGE,"E80.9.7.0"),sQuery(id+"F29.wireOp",EDGE,"E80.12.7.0"),sQuery(id+"F29.wireOp",EDGE,"E80.15.7.0"),sQuery(id+"F29.wireOp",EDGE,"E80.18.7.0"),sQuery(id+"F29.wireOp",EDGE,"E80.21.7.0"),sQuery(id+"F29.wireOp",EDGE,"E96.0.8.0"),sQuery(id+"F29.wireOp",EDGE,"E96.3.8.0"),sQuery(id+"F29.wireOp",EDGE,"E96.6.8.0"),sQuery(id+"F29.wireOp",EDGE,"E96.9.8.0"),sQuery(id+"F29.wireOp",EDGE,"E96.12.8.0"),sQuery(id+"F29.wireOp",EDGE,"E96.15.8.0"),sQuery(id+"F29.wireOp",EDGE,"E96.18.8.0"),sQuery(id+"F29.wireOp",EDGE,"E96.21.8.0"),sQuery(id+"F29.wireOp",EDGE,"E96.0.9.0"),sQuery(id+"F29.wireOp",EDGE,"E96.3.9.0"),sQuery(id+"F29.wireOp",EDGE,"E96.6.9.0"),sQuery(id+"F29.wireOp",EDGE,"E96.9.9.0"),sQuery(id+"F29.wireOp",EDGE,"E96.12.9.0"),sQuery(id+"F29.wireOp",EDGE,"E96.15.9.0"),sQuery(id+"F29.wireOp",EDGE,"E96.18.9.0"),sQuery(id+"F29.wireOp",EDGE,"E96.21.9.0"),sQuery(id+"F29.wireOp",EDGE,"E96.0.10.0"),sQuery(id+"F29.wireOp",EDGE,"E96.3.10.0"),sQuery(id+"F29.wireOp",EDGE,"E96.6.10.0"),sQuery(id+"F29.wireOp",EDGE,"E96.9.10.0"),sQuery(id+"F29.wireOp",EDGE,"E96.12.10.0"),sQuery(id+"F29.wireOp",EDGE,"E96.15.10.0"),sQuery(id+"F29.wireOp",EDGE,"E96.18.10.0"),sQuery(id+"F29.wireOp",EDGE,"E96.21.10.0"),sQuery(id+"F29.wireOp",EDGE,"E96.0.11.0"),sQuery(id+"F29.wireOp",EDGE,"E96.3.11.0"),sQuery(id+"F29.wireOp",EDGE,"E96.6.11.0"),sQuery(id+"F29.wireOp",EDGE,"E96.9.11.0"),sQuery(id+"F29.wireOp",EDGE,"E96.12.11.0"),sQuery(id+"F29.wireOp",EDGE,"E96.15.11.0"),sQuery(id+"F29.wireOp",EDGE,"E96.18.11.0"),sQuery(id+"F29.wireOp",EDGE,"E96.21.11.0"),sQuery(id+"F29.wireOp",EDGE,"E99"),sQuery(id+"F29.wireOp",EDGE,"E100")])],"isStart":true}),makeQuery(id+"F30.opExtrude","CAP_FACE",FACE,{"disambiguationData":[OSD([sQuery(id+"F29.wireOp",EDGE,"E83"),sQuery(id+"F29.wireOp",EDGE,"E84"),sQuery(id+"F29.wireOp",EDGE,"E85"),sQuery(id+"F29.wireOp",EDGE,"E86"),sQuery(id+"F29.wireOp",EDGE,"E87"),sQuery(id+"F29.wireOp",EDGE,"E88"),sQuery(id+"F29.wireOp",EDGE,"E89"),sQuery(id+"F29.wireOp",EDGE,"E90"),sQuery(id+"F29.wireOp",EDGE,"E91"),sQuery(id+"F29.wireOp",EDGE,"E92"),sQuery(id+"F29.wireOp",EDGE,"E93"),sQuery(id+"F29.wireOp",EDGE,"E94.1.0.0"),sQuery(id+"F29.wireOp",EDGE,"E94.1.0.1"),sQuery(id+"F29.wireOp",EDGE,"E94.1.0.2"),sQuery(id+"F29.wireOp",EDGE,"E94.1.0.3"),sQuery(id+"F29.wireOp",EDGE,"E94.1.0.4"),sQuery(id+"F29.wireOp",EDGE,"E94.1.0.5"),sQuery(id+"F29.wireOp",EDGE,"E94.1.0.6"),sQuery(id+"F29.wireOp",EDGE,"E94.1.0.7"),sQuery(id+"F29.wireOp",EDGE,"E94.2.0.0"),sQuery(id+"F29.wireOp",EDGE,"E94.2.0.1"),sQuery(id+"F29.wireOp",EDGE,"E94.2.0.2"),sQuery(id+"F29.wireOp",EDGE,"E94.2.0.3"),sQuery(id+"F29.wireOp",EDGE,"E94.2.0.4"),sQuery(id+"F29.wireOp",EDGE,"E94.2.0.5"),sQuery(id+"F29.wireOp",EDGE,"E94.2.0.6"),sQuery(id+"F29.wireOp",EDGE,"E94.2.0.7"),sQuery(id+"F29.wireOp",EDGE,"E95.0.3.0"),sQuery(id+"F29.wireOp",EDGE,"E95.3.3.0"),sQuery(id+"F29.wireOp",EDGE,"E95.6.3.0"),sQuery(id+"F29.wireOp",EDGE,"E95.9.3.0"),sQuery(id+"F29.wireOp",EDGE,"E95.12.3.0"),sQuery(id+"F29.wireOp",EDGE,"E95.15.3.0"),sQuery(id+"F29.wireOp",EDGE,"E95.18.3.0"),sQuery(id+"F29.wireOp",EDGE,"E95.21.3.0"),sQuery(id+"F29.wireOp",EDGE,"E95.0.4.0"),sQuery(id+"F29.wireOp",EDGE,"E95.3.4.0"),sQuery(id+"F29.wireOp",EDGE,"E95.6.4.0"),sQuery(id+"F29.wireOp",EDGE,"E95.9.4.0"),sQuery(id+"F29.wireOp",EDGE,"E95.12.4.0"),sQuery(id+"F29.wireOp",EDGE,"E95.15.4.0"),sQuery(id+"F29.wireOp",EDGE,"E95.18.4.0"),sQuery(id+"F29.wireOp",EDGE,"E95.21.4.0"),sQuery(id+"F29.wireOp",EDGE,"E95.0.5.0"),sQuery(id+"F29.wireOp",EDGE,"E95.3.5.0"),sQuery(id+"F29.wireOp",EDGE,"E95.6.5.0"),sQuery(id+"F29.wireOp",EDGE,"E95.9.5.0"),sQuery(id+"F29.wireOp",EDGE,"E95.12.5.0"),sQuery(id+"F29.wireOp",EDGE,"E95.15.5.0"),sQuery(id+"F29.wireOp",EDGE,"E95.18.5.0"),sQuery(id+"F29.wireOp",EDGE,"E95.21.5.0"),sQuery(id+"F29.wireOp",EDGE,"E97.0"),sQuery(id+"F29.wireOp",EDGE,"E98.0.6.0"),sQuery(id+"F29.wireOp",EDGE,"E98.3.6.0"),sQuery(id+"F29.wireOp",EDGE,"E98.6.6.0"),sQuery(id+"F29.wireOp",EDGE,"E98.9.6.0"),sQuery(id+"F29.wireOp",EDGE,"E98.12.6.0"),sQuery(id+"F29.wireOp",EDGE,"E98.15.6.0"),sQuery(id+"F29.wireOp",EDGE,"E98.18.6.0"),sQuery(id+"F29.wireOp",EDGE,"E98.21.6.0"),sQuery(id+"F29.wireOp",EDGE,"E98.0.7.0"),sQuery(id+"F29.wireOp",EDGE,"E98.3.7.0"),sQuery(id+"F29.wireOp",EDGE,"E98.6.7.0"),sQuery(id+"F29.wireOp",EDGE,"E98.9.7.0"),sQuery(id+"F29.wireOp",EDGE,"E98.12.7.0"),sQuery(id+"F29.wireOp",EDGE,"E98.15.7.0"),sQuery(id+"F29.wireOp",EDGE,"E98.18.7.0"),sQuery(id+"F29.wireOp",EDGE,"E98.21.7.0"),sQuery(id+"F29.wireOp",EDGE,"E98.0.8.0"),sQuery(id+"F29.wireOp",EDGE,"E98.3.8.0"),sQuery(id+"F29.wireOp",EDGE,"E98.6.8.0"),sQuery(id+"F29.wireOp",EDGE,"E98.9.8.0"),sQuery(id+"F29.wireOp",EDGE,"E98.12.8.0"),sQuery(id+"F29.wireOp",EDGE,"E98.15.8.0"),sQuery(id+"F29.wireOp",EDGE,"E98.18.8.0"),sQuery(id+"F29.wireOp",EDGE,"E98.21.8.0"),sQuery(id+"F29.wireOp",EDGE,"E98.0.9.0"),sQuery(id+"F29.wireOp",EDGE,"E98.3.9.0"),sQuery(id+"F29.wireOp",EDGE,"E98.6.9.0"),sQuery(id+"F29.wireOp",EDGE,"E98.9.9.0"),sQuery(id+"F29.wireOp",EDGE,"E98.12.9.0"),sQuery(id+"F29.wireOp",EDGE,"E98.15.9.0"),sQuery(id+"F29.wireOp",EDGE,"E98.18.9.0"),sQuery(id+"F29.wireOp",EDGE,"E98.21.9.0"),sQuery(id+"F29.wireOp",EDGE,"E98.0.10.0"),sQuery(id+"F29.wireOp",EDGE,"E98.3.10.0"),sQuery(id+"F29.wireOp",EDGE,"E98.6.10.0"),sQuery(id+"F29.wireOp",EDGE,"E98.9.10.0"),sQuery(id+"F29.wireOp",EDGE,"E98.12.10.0"),sQuery(id+"F29.wireOp",EDGE,"E98.15.10.0"),sQuery(id+"F29.wireOp",EDGE,"E98.18.10.0"),sQuery(id+"F29.wireOp",EDGE,"E98.21.10.0"),sQuery(id+"F29.wireOp",EDGE,"E98.0.11.0"),sQuery(id+"F29.wireOp",EDGE,"E98.3.11.0"),sQuery(id+"F29.wireOp",EDGE,"E98.6.11.0"),sQuery(id+"F29.wireOp",EDGE,"E98.9.11.0"),sQuery(id+"F29.wireOp",EDGE,"E98.12.11.0"),sQuery(id+"F29.wireOp",EDGE,"E98.15.11.0"),sQuery(id+"F29.wireOp",EDGE,"E98.18.11.0"),sQuery(id+"F29.wireOp",EDGE,"E98.21.11.0"),sQuery(id+"F29.wireOp",EDGE,"E101"),sQuery(id+"F29.wireOp",EDGE,"E102")])],"isStart":true})]});
            extrude(context, id + "F43", {"entities" : qUnion([Q0]), "operationType" : NewBodyOperationType.ADD, "endBound" : BoundingType.UP_TO_SURFACE, "oppositeDirection" : true, "depth" : 25 * mm, "endBoundEntityFace" : qUnion([Q1]), "offsetDistance" : 25 * mm});
        }
        {
            var Q0;
            Q0=makeQuery(id+"F31.imprint","IMPRINT",FACE,{"disambiguationData":[TD([[makeQuery(id+"F31.imprint","IMPRINT",EDGE,{"derivedFrom":makeQuery(id+"F22.opExtrude","CAP_EDGE",EDGE,{"disambiguationData":[OSD([sQuery(id+"F21.wireOp",EDGE,"E51.0")])],"isStart":true})}),1.0]])]});
            var sketch = newSketch(context, id + "F44", { "sketchPlane" : qUnion([Q0])});
            skLineSegment(sketch, "E117", {"start": v(27.9, -97.46) * mm, "end": v(27.9, -99.49) * mm});
            skLineSegment(sketch, "E118", {"start": v(27.9, -99.49) * mm, "end": v(33.16, -99.49) * mm});
            skLineSegment(sketch, "E119", {"start": v(33.16, -99.49) * mm, "end": v(33.16, -107.49) * mm});
            skLineSegment(sketch, "E120", {"start": v(33.16, -117.51) * mm, "end": v(27.9, -117.51) * mm});
            skLineSegment(sketch, "E121", {"start": v(27.9, -117.51) * mm, "end": v(27.9, -119.54) * mm});
            skLineSegment(sketch, "E122", {"start": v(27.9, -119.54) * mm, "end": v(36.16, -119.54) * mm});
            skLineSegment(sketch, "E123", {"start": v(36.16, -119.54) * mm, "end": v(36.16, -97.46) * mm});
            skLineSegment(sketch, "E124", {"start": v(36.16, -97.46) * mm, "end": v(27.9, -97.46) * mm});
            skLineSegment(sketch, "E125", {"start": v(33.16, -107.49) * mm, "end": v(27.9, -107.49) * mm});
            skLineSegment(sketch, "E126", {"start": v(27.9, -107.49) * mm, "end": v(27.9, -109.51) * mm});
            skLineSegment(sketch, "E127", {"start": v(27.9, -109.51) * mm, "end": v(33.16, -109.51) * mm});
            skLineSegment(sketch, "E128.trimOffspring", {"start": v(33.16, -109.51) * mm, "end": v(33.16, -117.51) * mm});
            skLineSegment(sketch, "E129.0", {"start": v(26.9, -107) * mm, "end": v(26.9, -110) * mm, "construction": true});
            skLineSegment(sketch, "E130", {"start": v(26.9, -108.5) * mm, "end": v(33.2, -108.5) * mm, "construction": true});
            skSolve(sketch);
        }
        {
            var Q0;
            Q0 = qSketchRegion(id + "F44", true);
            var Q1;
            Q1=makeQuery(id+"F43.boolean.opBoolean","MERGE",FACE,{"derivedFrom":[makeQuery(id+"F30.boolean.opBoolean","MERGE",FACE,{"derivedFrom":[makeQuery(id+"F22.opExtrude","CAP_FACE",FACE,{"disambiguationData":[OSD([sQuery(id+"F21.wireOp",EDGE,"E51.0"),sQuery(id+"F21.wireOp",EDGE,"E52.0"),sQuery(id+"F21.wireOp",EDGE,"E53.0"),sQuery(id+"F21.wireOp",EDGE,"E54.0"),sQuery(id+"F21.wireOp",EDGE,"E55.0"),sQuery(id+"F21.wireOp",EDGE,"E56"),sQuery(id+"F21.wireOp",EDGE,"E57"),sQuery(id+"F21.wireOp",EDGE,"E58"),sQuery(id+"F21.wireOp",EDGE,"E59.0"),sQuery(id+"F21.wireOp",EDGE,"E59.1"),sQuery(id+"F21.wireOp",EDGE,"E59.2"),sQuery(id+"F21.wireOp",EDGE,"E59.3"),sQuery(id+"F21.wireOp",EDGE,"E59.4"),sQuery(id+"F21.wireOp",EDGE,"E59.5"),sQuery(id+"F21.wireOp",EDGE,"E59.6"),sQuery(id+"F21.wireOp",EDGE,"E60")])],"isStart":false}),makeQuery(id+"F30.opExtrude","CAP_FACE",FACE,{"disambiguationData":[OSD([sQuery(id+"F29.wireOp",EDGE,"E67.0"),sQuery(id+"F29.wireOp",EDGE,"E68"),sQuery(id+"F29.wireOp",EDGE,"E69"),sQuery(id+"F29.wireOp",EDGE,"E70"),sQuery(id+"F29.wireOp",EDGE,"E71"),sQuery(id+"F29.wireOp",EDGE,"E72"),sQuery(id+"F29.wireOp",EDGE,"E73"),sQuery(id+"F29.wireOp",EDGE,"E74"),sQuery(id+"F29.wireOp",EDGE,"E75"),sQuery(id+"F29.wireOp",EDGE,"E76"),sQuery(id+"F29.wireOp",EDGE,"E77"),sQuery(id+"F29.wireOp",EDGE,"E78"),sQuery(id+"F29.wireOp",EDGE,"E79.1.0.0"),sQuery(id+"F29.wireOp",EDGE,"E79.1.0.1"),sQuery(id+"F29.wireOp",EDGE,"E79.1.0.2"),sQuery(id+"F29.wireOp",EDGE,"E79.1.0.3"),sQuery(id+"F29.wireOp",EDGE,"E79.1.0.4"),sQuery(id+"F29.wireOp",EDGE,"E79.1.0.5"),sQuery(id+"F29.wireOp",EDGE,"E79.1.0.6"),sQuery(id+"F29.wireOp",EDGE,"E79.1.0.7"),sQuery(id+"F29.wireOp",EDGE,"E79.2.0.0"),sQuery(id+"F29.wireOp",EDGE,"E79.2.0.1"),sQuery(id+"F29.wireOp",EDGE,"E79.2.0.2"),sQuery(id+"F29.wireOp",EDGE,"E79.2.0.3"),sQuery(id+"F29.wireOp",EDGE,"E79.2.0.4"),sQuery(id+"F29.wireOp",EDGE,"E79.2.0.5"),sQuery(id+"F29.wireOp",EDGE,"E79.2.0.6"),sQuery(id+"F29.wireOp",EDGE,"E79.2.0.7"),sQuery(id+"F29.wireOp",EDGE,"E80.0.3.0"),sQuery(id+"F29.wireOp",EDGE,"E80.3.3.0"),sQuery(id+"F29.wireOp",EDGE,"E80.6.3.0"),sQuery(id+"F29.wireOp",EDGE,"E80.9.3.0"),sQuery(id+"F29.wireOp",EDGE,"E80.12.3.0"),sQuery(id+"F29.wireOp",EDGE,"E80.15.3.0"),sQuery(id+"F29.wireOp",EDGE,"E80.18.3.0"),sQuery(id+"F29.wireOp",EDGE,"E80.21.3.0"),sQuery(id+"F29.wireOp",EDGE,"E80.0.4.0"),sQuery(id+"F29.wireOp",EDGE,"E80.3.4.0"),sQuery(id+"F29.wireOp",EDGE,"E80.6.4.0"),sQuery(id+"F29.wireOp",EDGE,"E80.9.4.0"),sQuery(id+"F29.wireOp",EDGE,"E80.12.4.0"),sQuery(id+"F29.wireOp",EDGE,"E80.15.4.0"),sQuery(id+"F29.wireOp",EDGE,"E80.18.4.0"),sQuery(id+"F29.wireOp",EDGE,"E80.21.4.0"),sQuery(id+"F29.wireOp",EDGE,"E80.0.5.0"),sQuery(id+"F29.wireOp",EDGE,"E80.3.5.0"),sQuery(id+"F29.wireOp",EDGE,"E80.6.5.0"),sQuery(id+"F29.wireOp",EDGE,"E80.9.5.0"),sQuery(id+"F29.wireOp",EDGE,"E80.12.5.0"),sQuery(id+"F29.wireOp",EDGE,"E80.15.5.0"),sQuery(id+"F29.wireOp",EDGE,"E80.18.5.0"),sQuery(id+"F29.wireOp",EDGE,"E80.21.5.0"),sQuery(id+"F29.wireOp",EDGE,"E80.0.6.0"),sQuery(id+"F29.wireOp",EDGE,"E80.3.6.0"),sQuery(id+"F29.wireOp",EDGE,"E80.6.6.0"),sQuery(id+"F29.wireOp",EDGE,"E80.9.6.0"),sQuery(id+"F29.wireOp",EDGE,"E80.12.6.0"),sQuery(id+"F29.wireOp",EDGE,"E80.15.6.0"),sQuery(id+"F29.wireOp",EDGE,"E80.18.6.0"),sQuery(id+"F29.wireOp",EDGE,"E80.21.6.0"),sQuery(id+"F29.wireOp",EDGE,"E80.0.7.0"),sQuery(id+"F29.wireOp",EDGE,"E80.3.7.0"),sQuery(id+"F29.wireOp",EDGE,"E80.6.7.0"),sQuery(id+"F29.wireOp",EDGE,"E80.9.7.0"),sQuery(id+"F29.wireOp",EDGE,"E80.12.7.0"),sQuery(id+"F29.wireOp",EDGE,"E80.15.7.0"),sQuery(id+"F29.wireOp",EDGE,"E80.18.7.0"),sQuery(id+"F29.wireOp",EDGE,"E80.21.7.0"),sQuery(id+"F29.wireOp",EDGE,"E96.0.8.0"),sQuery(id+"F29.wireOp",EDGE,"E96.3.8.0"),sQuery(id+"F29.wireOp",EDGE,"E96.6.8.0"),sQuery(id+"F29.wireOp",EDGE,"E96.9.8.0"),sQuery(id+"F29.wireOp",EDGE,"E96.12.8.0"),sQuery(id+"F29.wireOp",EDGE,"E96.15.8.0"),sQuery(id+"F29.wireOp",EDGE,"E96.18.8.0"),sQuery(id+"F29.wireOp",EDGE,"E96.21.8.0"),sQuery(id+"F29.wireOp",EDGE,"E96.0.9.0"),sQuery(id+"F29.wireOp",EDGE,"E96.3.9.0"),sQuery(id+"F29.wireOp",EDGE,"E96.6.9.0"),sQuery(id+"F29.wireOp",EDGE,"E96.9.9.0"),sQuery(id+"F29.wireOp",EDGE,"E96.12.9.0"),sQuery(id+"F29.wireOp",EDGE,"E96.15.9.0"),sQuery(id+"F29.wireOp",EDGE,"E96.18.9.0"),sQuery(id+"F29.wireOp",EDGE,"E96.21.9.0"),sQuery(id+"F29.wireOp",EDGE,"E96.0.10.0"),sQuery(id+"F29.wireOp",EDGE,"E96.3.10.0"),sQuery(id+"F29.wireOp",EDGE,"E96.6.10.0"),sQuery(id+"F29.wireOp",EDGE,"E96.9.10.0"),sQuery(id+"F29.wireOp",EDGE,"E96.12.10.0"),sQuery(id+"F29.wireOp",EDGE,"E96.15.10.0"),sQuery(id+"F29.wireOp",EDGE,"E96.18.10.0"),sQuery(id+"F29.wireOp",EDGE,"E96.21.10.0"),sQuery(id+"F29.wireOp",EDGE,"E96.0.11.0"),sQuery(id+"F29.wireOp",EDGE,"E96.3.11.0"),sQuery(id+"F29.wireOp",EDGE,"E96.6.11.0"),sQuery(id+"F29.wireOp",EDGE,"E96.9.11.0"),sQuery(id+"F29.wireOp",EDGE,"E96.12.11.0"),sQuery(id+"F29.wireOp",EDGE,"E96.15.11.0"),sQuery(id+"F29.wireOp",EDGE,"E96.18.11.0"),sQuery(id+"F29.wireOp",EDGE,"E96.21.11.0"),sQuery(id+"F29.wireOp",EDGE,"E99"),sQuery(id+"F29.wireOp",EDGE,"E100")])],"isStart":false}),makeQuery(id+"F30.opExtrude","CAP_FACE",FACE,{"disambiguationData":[OSD([sQuery(id+"F29.wireOp",EDGE,"E83"),sQuery(id+"F29.wireOp",EDGE,"E84"),sQuery(id+"F29.wireOp",EDGE,"E85"),sQuery(id+"F29.wireOp",EDGE,"E86"),sQuery(id+"F29.wireOp",EDGE,"E87"),sQuery(id+"F29.wireOp",EDGE,"E88"),sQuery(id+"F29.wireOp",EDGE,"E89"),sQuery(id+"F29.wireOp",EDGE,"E90"),sQuery(id+"F29.wireOp",EDGE,"E91"),sQuery(id+"F29.wireOp",EDGE,"E92"),sQuery(id+"F29.wireOp",EDGE,"E93"),sQuery(id+"F29.wireOp",EDGE,"E94.1.0.0"),sQuery(id+"F29.wireOp",EDGE,"E94.1.0.1"),sQuery(id+"F29.wireOp",EDGE,"E94.1.0.2"),sQuery(id+"F29.wireOp",EDGE,"E94.1.0.3"),sQuery(id+"F29.wireOp",EDGE,"E94.1.0.4"),sQuery(id+"F29.wireOp",EDGE,"E94.1.0.5"),sQuery(id+"F29.wireOp",EDGE,"E94.1.0.6"),sQuery(id+"F29.wireOp",EDGE,"E94.1.0.7"),sQuery(id+"F29.wireOp",EDGE,"E94.2.0.0"),sQuery(id+"F29.wireOp",EDGE,"E94.2.0.1"),sQuery(id+"F29.wireOp",EDGE,"E94.2.0.2"),sQuery(id+"F29.wireOp",EDGE,"E94.2.0.3"),sQuery(id+"F29.wireOp",EDGE,"E94.2.0.4"),sQuery(id+"F29.wireOp",EDGE,"E94.2.0.5"),sQuery(id+"F29.wireOp",EDGE,"E94.2.0.6"),sQuery(id+"F29.wireOp",EDGE,"E94.2.0.7"),sQuery(id+"F29.wireOp",EDGE,"E95.0.3.0"),sQuery(id+"F29.wireOp",EDGE,"E95.3.3.0"),sQuery(id+"F29.wireOp",EDGE,"E95.6.3.0"),sQuery(id+"F29.wireOp",EDGE,"E95.9.3.0"),sQuery(id+"F29.wireOp",EDGE,"E95.12.3.0"),sQuery(id+"F29.wireOp",EDGE,"E95.15.3.0"),sQuery(id+"F29.wireOp",EDGE,"E95.18.3.0"),sQuery(id+"F29.wireOp",EDGE,"E95.21.3.0"),sQuery(id+"F29.wireOp",EDGE,"E95.0.4.0"),sQuery(id+"F29.wireOp",EDGE,"E95.3.4.0"),sQuery(id+"F29.wireOp",EDGE,"E95.6.4.0"),sQuery(id+"F29.wireOp",EDGE,"E95.9.4.0"),sQuery(id+"F29.wireOp",EDGE,"E95.12.4.0"),sQuery(id+"F29.wireOp",EDGE,"E95.15.4.0"),sQuery(id+"F29.wireOp",EDGE,"E95.18.4.0"),sQuery(id+"F29.wireOp",EDGE,"E95.21.4.0"),sQuery(id+"F29.wireOp",EDGE,"E95.0.5.0"),sQuery(id+"F29.wireOp",EDGE,"E95.3.5.0"),sQuery(id+"F29.wireOp",EDGE,"E95.6.5.0"),sQuery(id+"F29.wireOp",EDGE,"E95.9.5.0"),sQuery(id+"F29.wireOp",EDGE,"E95.12.5.0"),sQuery(id+"F29.wireOp",EDGE,"E95.15.5.0"),sQuery(id+"F29.wireOp",EDGE,"E95.18.5.0"),sQuery(id+"F29.wireOp",EDGE,"E95.21.5.0"),sQuery(id+"F29.wireOp",EDGE,"E97.0"),sQuery(id+"F29.wireOp",EDGE,"E98.0.6.0"),sQuery(id+"F29.wireOp",EDGE,"E98.3.6.0"),sQuery(id+"F29.wireOp",EDGE,"E98.6.6.0"),sQuery(id+"F29.wireOp",EDGE,"E98.9.6.0"),sQuery(id+"F29.wireOp",EDGE,"E98.12.6.0"),sQuery(id+"F29.wireOp",EDGE,"E98.15.6.0"),sQuery(id+"F29.wireOp",EDGE,"E98.18.6.0"),sQuery(id+"F29.wireOp",EDGE,"E98.21.6.0"),sQuery(id+"F29.wireOp",EDGE,"E101"),sQuery(id+"F29.wireOp",EDGE,"E102")])],"isStart":false})]}),makeQuery(id+"F43.opExtrude","CAP_FACE",FACE,{"disambiguationData":[OSD([sQuery(id+"F42.wireOp",EDGE,"E111.bottom"),sQuery(id+"F42.wireOp",EDGE,"E111.top"),sQuery(id+"F42.wireOp",EDGE,"E111.left"),sQuery(id+"F42.wireOp",EDGE,"E111.right")])],"isStart":true}),makeQuery(id+"F43.opExtrude","CAP_FACE",FACE,{"disambiguationData":[OSD([sQuery(id+"F42.wireOp",EDGE,"E112.MirrorCS"),sQuery(id+"F42.wireOp",EDGE,"E113.MirrorCS"),sQuery(id+"F42.wireOp",EDGE,"E114.MirrorCS"),sQuery(id+"F42.wireOp",EDGE,"E115.MirrorCS")])],"isStart":true})]});
            extrude(context, id + "F45", {"entities" : qUnion([Q0]), "endBound" : BoundingType.UP_TO_SURFACE, "oppositeDirection" : true, "depth" : 25 * mm, "endBoundEntityFace" : qUnion([Q1]), "offsetDistance" : 25 * mm});
        }
        {
            var Q0;
            Q0=makeQuery(id+"F45.opExtrude","CAP_FACE",FACE,{"disambiguationData":[OSD([sQuery(id+"F44.wireOp",EDGE,"E117"),sQuery(id+"F44.wireOp",EDGE,"E118"),sQuery(id+"F44.wireOp",EDGE,"E119"),sQuery(id+"F44.wireOp",EDGE,"E120"),sQuery(id+"F44.wireOp",EDGE,"E121"),sQuery(id+"F44.wireOp",EDGE,"E122"),sQuery(id+"F44.wireOp",EDGE,"E123"),sQuery(id+"F44.wireOp",EDGE,"E124"),sQuery(id+"F44.wireOp",EDGE,"E125"),sQuery(id+"F44.wireOp",EDGE,"E126"),sQuery(id+"F44.wireOp",EDGE,"E127"),sQuery(id+"F44.wireOp",EDGE,"E128.trimOffspring")])],"isStart":true});
            var sketch = newSketch(context, id + "F46", { "sketchPlane" : qUnion([Q0])});
            skLineSegment(sketch, "E131.bottom", {"start": v(25.16, -119.54) * mm, "end": v(36.16, -119.54) * mm});
            skLineSegment(sketch, "E131.top", {"start": v(25.16, -97.46) * mm, "end": v(36.16, -97.46) * mm});
            skLineSegment(sketch, "E131.left", {"start": v(25.16, -119.54) * mm, "end": v(25.16, -97.46) * mm});
            skLineSegment(sketch, "E131.right", {"start": v(36.16, -119.54) * mm, "end": v(36.16, -97.46) * mm});
            skSolve(sketch);
        }
        {
            var Q0;
            Q0 = qSketchRegion(id + "F46", true);
            extrude(context, id + "F47", {"entities" : qUnion([Q0]), "operationType" : NewBodyOperationType.ADD, "depth" : 3 * mm, "offsetDistance" : 25 * mm});
        }
        {
            var Q0;
            Q0=makeQuery(id+"F47.opExtrude","CAP_FACE",FACE,{"disambiguationData":[OSD([sQuery(id+"F46.wireOp",EDGE,"E131.bottom"),sQuery(id+"F46.wireOp",EDGE,"E131.top"),sQuery(id+"F46.wireOp",EDGE,"E131.left"),sQuery(id+"F46.wireOp",EDGE,"E131.right")])],"isStart":true});
            var sketch = newSketch(context, id + "F48", { "sketchPlane" : qUnion([Q0])});
            skLineSegment(sketch, "E132.bottom", {"start": v(-28.66, -114.51) * mm, "end": v(-25.16, -114.51) * mm});
            skLineSegment(sketch, "E132.top", {"start": v(-28.66, -112.51) * mm, "end": v(-25.16, -112.51) * mm});
            skLineSegment(sketch, "E132.left", {"start": v(-28.66, -114.51) * mm, "end": v(-28.66, -112.51) * mm});
            skLineSegment(sketch, "E132.right", {"start": v(-25.16, -114.51) * mm, "end": v(-25.16, -112.51) * mm});
            skPoint(sketch, "E132.middle", {"position": v(-26.91, -113.51) * mm});
            skLineSegment(sketch, "E133.0", {"start": v(-25.9, -106) * mm, "end": v(-25.9, -111) * mm, "construction": true});
            skLineSegment(sketch, "E134.0", {"start": v(-33.16, -109.51) * mm, "end": v(-33.16, -117.51) * mm, "construction": true});
            skLineSegment(sketch, "E135", {"start": v(-33.16, -113.51) * mm, "end": v(-28.66, -113.51) * mm, "construction": true});
            skLineSegment(sketch, "E136", {"start": v(-25.9, -108.5) * mm, "end": v(-34.93, -108.5) * mm, "construction": true});
            skLineSegment(sketch, "E137.MirrorCS", {"start": v(-33.16, -103.49) * mm, "end": v(-28.66, -103.49) * mm, "construction": true});
            skLineSegment(sketch, "E138.MirrorCS", {"start": v(-28.66, -104.49) * mm, "end": v(-25.16, -104.49) * mm});
            skPoint(sketch, "E139.MirrorP", {"position": v(-26.91, -103.49) * mm});
            skLineSegment(sketch, "E140.MirrorCS", {"start": v(-28.66, -102.49) * mm, "end": v(-25.16, -102.49) * mm});
            skLineSegment(sketch, "E141.MirrorCS", {"start": v(-25.16, -102.49) * mm, "end": v(-25.16, -104.49) * mm});
            skLineSegment(sketch, "E142.MirrorCS", {"start": v(-28.66, -102.49) * mm, "end": v(-28.66, -104.49) * mm});
            skSolve(sketch);
        }
        {
            var Q0;
            Q0 = qSketchRegion(id + "F48", true);
            var Q1;
            Q1=makeQuery(id+"F45.opExtrude","CAP_FACE",FACE,{"disambiguationData":[OSD([sQuery(id+"F44.wireOp",EDGE,"E117"),sQuery(id+"F44.wireOp",EDGE,"E118"),sQuery(id+"F44.wireOp",EDGE,"E119"),sQuery(id+"F44.wireOp",EDGE,"E120"),sQuery(id+"F44.wireOp",EDGE,"E121"),sQuery(id+"F44.wireOp",EDGE,"E122"),sQuery(id+"F44.wireOp",EDGE,"E123"),sQuery(id+"F44.wireOp",EDGE,"E124"),sQuery(id+"F44.wireOp",EDGE,"E125"),sQuery(id+"F44.wireOp",EDGE,"E126"),sQuery(id+"F44.wireOp",EDGE,"E127"),sQuery(id+"F44.wireOp",EDGE,"E128.trimOffspring")])],"isStart":false});
            extrude(context, id + "F49", {"entities" : qUnion([Q0]), "operationType" : NewBodyOperationType.ADD, "endBound" : BoundingType.UP_TO_SURFACE, "depth" : 25 * mm, "endBoundEntityFace" : qUnion([Q1]), "offsetDistance" : 25 * mm});
        }
        {
            var Q0;
            Q0=makeQuery(id+"F47.boolean.opBoolean","MERGE",EDGE,{"derivedFrom":[makeQuery(id+"F45.opExtrude","SWEPT_EDGE",EDGE,{"disambiguationData":[OSD([sQuery(id+"F44.wireOp",EDGE,"E123"),sQuery(id+"F44.wireOp",EDGE,"E124")])]}),makeQuery(id+"F47.opExtrude","SWEPT_EDGE",EDGE,{"disambiguationData":[OSD([sQuery(id+"F46.wireOp",EDGE,"E131.top"),sQuery(id+"F46.wireOp",EDGE,"E131.right")])]})]});
            var Q1;
            Q1=makeQuery(id+"F47.boolean.opBoolean","MERGE",EDGE,{"derivedFrom":[makeQuery(id+"F45.opExtrude","SWEPT_EDGE",EDGE,{"disambiguationData":[OSD([sQuery(id+"F44.wireOp",EDGE,"E122"),sQuery(id+"F44.wireOp",EDGE,"E123")])]}),makeQuery(id+"F47.opExtrude","SWEPT_EDGE",EDGE,{"disambiguationData":[OSD([sQuery(id+"F46.wireOp",EDGE,"E131.bottom"),sQuery(id+"F46.wireOp",EDGE,"E131.right")])]})]});
            fillet(context, id + "F50", {"entities" : qUnion([Q0, Q1]), "radius" : 5 * mm, "tangentPropagation" : true, "allowEdgeOverflow" : false});
        }
    });
